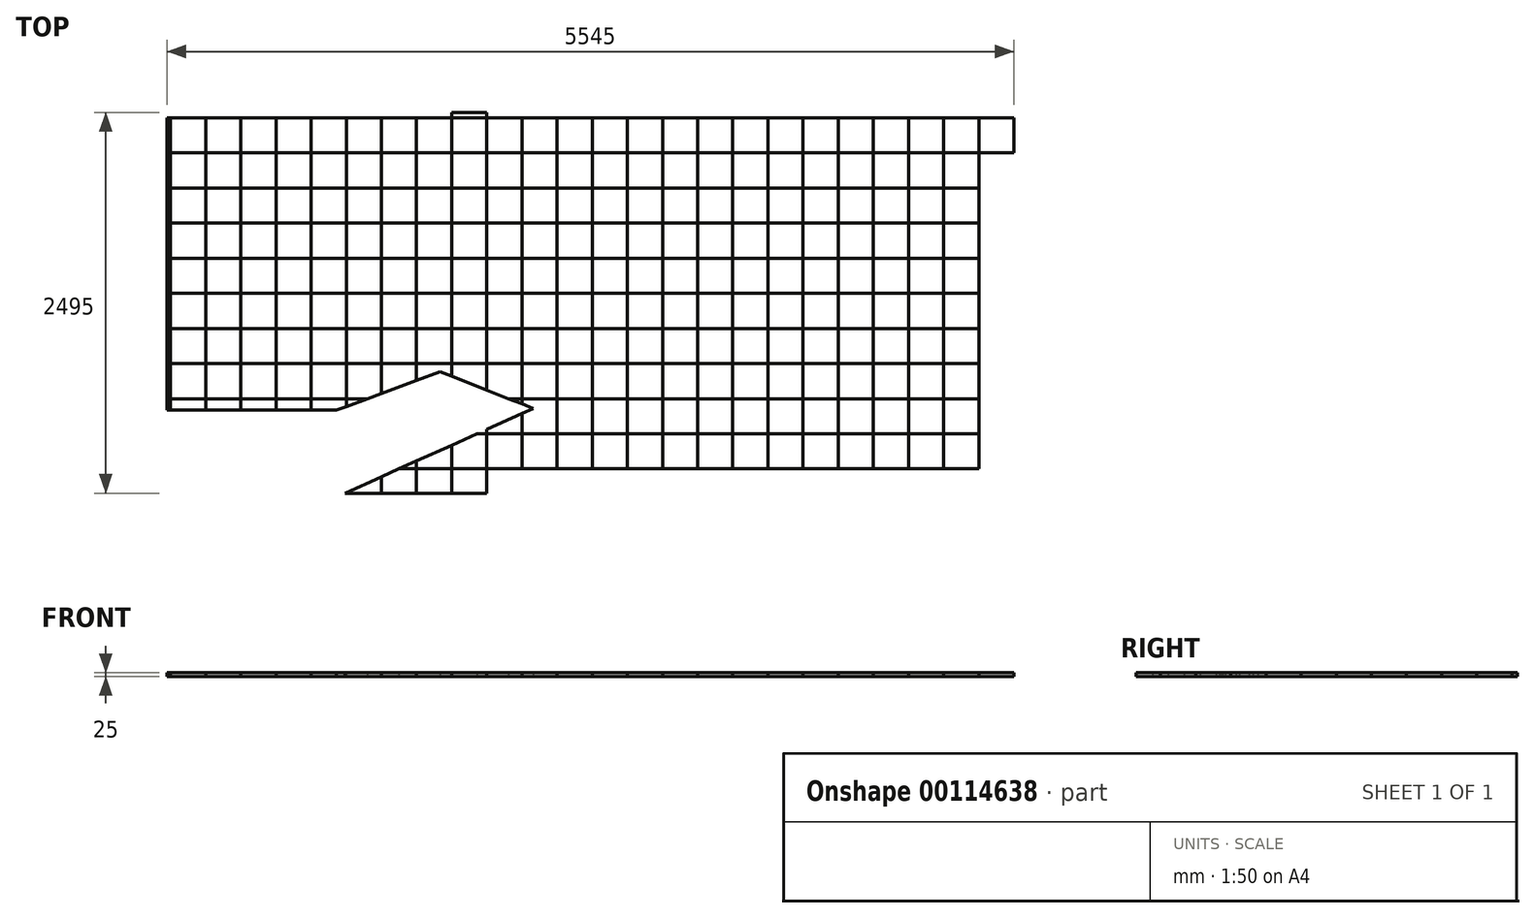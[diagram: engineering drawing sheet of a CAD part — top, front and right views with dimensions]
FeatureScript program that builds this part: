
annotation { "Feature Type Name" : "Feature", "Feature Type Description" : "" }
export const myFeature = defineFeature(function(context is Context, id is Id, definition is map)
    precondition{}
    {
        {
            var Q0;
            Q0=qCreatedBy(makeId("Top.planeOp"),FACE);
            var sketch = newSketch(context, id + "F0", { "sketchPlane" : qUnion([Q0])});
            skLineSegment(sketch, "E0.bottom", {"start": v(2772.5, -1247.5) * mm, "end": v(-1606.57, -1247.5) * mm});
            skLineSegment(sketch, "E0.top", {"start": v(2772.5, 1247.5) * mm, "end": v(-2772.5, 1247.5) * mm});
            skLineSegment(sketch, "E0.left", {"start": v(2772.5, -1247.5) * mm, "end": v(2772.5, 1247.5) * mm});
            skLineSegment(sketch, "E0.right", {"start": v(-2772.5, -702.5) * mm, "end": v(-2772.5, 1247.5) * mm});
            skPoint(sketch, "E0.middle", {"position": v(0, 0) * mm});
            skLineSegment(sketch, "E1", {"start": v(-2772.5, -702.5) * mm, "end": v(-1662.5, -702.5) * mm});
            skLineSegment(sketch, "E2", {"start": v(-1662.5, -702.5) * mm, "end": v(-982.3, -451.6) * mm});
            skLineSegment(sketch, "E3", {"start": v(-982.3, -451.6) * mm, "end": v(-372.7, -691.22) * mm});
            skLineSegment(sketch, "E4", {"start": v(-372.7, -691.22) * mm, "end": v(-1606.57, -1247.5) * mm});
            skPoint(sketch, "E5.orphan", {"position": v(-2772.5, -1247.5) * mm});
            skLineSegment(sketch, "E6.right", {"start": v(-2772.5, 1247.5) * mm, "end": v(-2772.5, 1217.5) * mm});
            skPoint(sketch, "E7.endSnap0", {"position": v(582.97, -1247.5) * mm});
            skLineSegment(sketch, "E8.bottom", {"start": v(-2772.5, 1247.5) * mm, "end": v(2772.5, 1247.5) * mm});
            skLineSegment(sketch, "E8.top", {"start": v(-2772.5, 1212.5) * mm, "end": v(2772.5, 1212.5) * mm});
            skLineSegment(sketch, "E8.left", {"start": v(-2772.5, 1247.5) * mm, "end": v(-2772.5, 1212.5) * mm});
            skLineSegment(sketch, "E8.right", {"start": v(2772.5, 1247.5) * mm, "end": v(2772.5, 1212.5) * mm});
            skLineSegment(sketch, "E9.bottom", {"start": v(2772.5, 1247.5) * mm, "end": v(2542.5, 1247.5) * mm});
            skLineSegment(sketch, "E9.top", {"start": v(2772.5, -1247.5) * mm, "end": v(2542.5, -1247.5) * mm});
            skLineSegment(sketch, "E9.left", {"start": v(2772.5, 1247.5) * mm, "end": v(2772.5, -1247.5) * mm});
            skLineSegment(sketch, "E9.right", {"start": v(2542.5, 1247.5) * mm, "end": v(2542.5, -1247.5) * mm});
            skLineSegment(sketch, "E10.bottom", {"start": v(2542.5, 1247.5) * mm, "end": v(2312.5, 1247.5) * mm});
            skLineSegment(sketch, "E10.top", {"start": v(2542.5, -1247.5) * mm, "end": v(2312.5, -1247.5) * mm});
            skLineSegment(sketch, "E10.right", {"start": v(2312.5, 1247.5) * mm, "end": v(2312.5, -1247.5) * mm});
            skLineSegment(sketch, "E11.bottom", {"start": v(2312.5, 1247.5) * mm, "end": v(2082.5, 1247.5) * mm});
            skLineSegment(sketch, "E11.top", {"start": v(2312.5, -1247.5) * mm, "end": v(2082.5, -1247.5) * mm});
            skLineSegment(sketch, "E11.right", {"start": v(2082.5, 1247.5) * mm, "end": v(2082.5, -1247.5) * mm});
            skLineSegment(sketch, "E12.bottom", {"start": v(2082.5, 1247.5) * mm, "end": v(1852.5, 1247.5) * mm});
            skLineSegment(sketch, "E12.top", {"start": v(2082.5, -1247.5) * mm, "end": v(1852.5, -1247.5) * mm});
            skLineSegment(sketch, "E12.right", {"start": v(1852.5, 1247.5) * mm, "end": v(1852.5, -1247.5) * mm});
            skLineSegment(sketch, "E13.bottom", {"start": v(1852.5, 1247.5) * mm, "end": v(1622.5, 1247.5) * mm});
            skLineSegment(sketch, "E13.top", {"start": v(1852.5, -1247.5) * mm, "end": v(1622.5, -1247.5) * mm});
            skLineSegment(sketch, "E13.right", {"start": v(1622.5, 1247.5) * mm, "end": v(1622.5, -1247.5) * mm});
            skLineSegment(sketch, "E14.bottom", {"start": v(1622.5, 1247.5) * mm, "end": v(1392.5, 1247.5) * mm});
            skLineSegment(sketch, "E14.top", {"start": v(1622.5, -1247.5) * mm, "end": v(1392.5, -1247.5) * mm});
            skLineSegment(sketch, "E14.right", {"start": v(1392.5, 1247.5) * mm, "end": v(1392.5, -1247.5) * mm});
            skLineSegment(sketch, "E15.bottom", {"start": v(1392.5, 1247.5) * mm, "end": v(1162.5, 1247.5) * mm});
            skLineSegment(sketch, "E15.top", {"start": v(1392.5, -1247.5) * mm, "end": v(1162.5, -1247.5) * mm});
            skLineSegment(sketch, "E15.right", {"start": v(1162.5, 1247.5) * mm, "end": v(1162.5, -1247.5) * mm});
            skLineSegment(sketch, "E16.bottom", {"start": v(1162.5, 1247.5) * mm, "end": v(932.5, 1247.5) * mm});
            skLineSegment(sketch, "E16.top", {"start": v(1162.5, -1247.5) * mm, "end": v(932.5, -1247.5) * mm});
            skLineSegment(sketch, "E16.right", {"start": v(932.5, 1247.5) * mm, "end": v(932.5, -1247.5) * mm});
            skLineSegment(sketch, "E17.bottom", {"start": v(932.5, 1247.5) * mm, "end": v(702.5, 1247.5) * mm});
            skLineSegment(sketch, "E17.top", {"start": v(932.5, -1247.5) * mm, "end": v(702.5, -1247.5) * mm});
            skLineSegment(sketch, "E17.right", {"start": v(702.5, 1247.5) * mm, "end": v(702.5, -1247.5) * mm});
            skLineSegment(sketch, "E18.bottom", {"start": v(702.5, 1247.5) * mm, "end": v(472.5, 1247.5) * mm});
            skLineSegment(sketch, "E18.top", {"start": v(702.5, -1247.5) * mm, "end": v(472.5, -1247.5) * mm});
            skLineSegment(sketch, "E18.right", {"start": v(472.5, 1247.5) * mm, "end": v(472.5, -1247.5) * mm});
            skLineSegment(sketch, "E19.bottom", {"start": v(472.5, 1247.5) * mm, "end": v(242.5, 1247.5) * mm});
            skLineSegment(sketch, "E19.top", {"start": v(472.5, -1247.5) * mm, "end": v(242.5, -1247.5) * mm});
            skLineSegment(sketch, "E19.right", {"start": v(242.5, 1247.5) * mm, "end": v(242.5, -1247.5) * mm});
            skLineSegment(sketch, "E20.bottom", {"start": v(242.5, 1247.5) * mm, "end": v(12.5, 1247.5) * mm});
            skLineSegment(sketch, "E20.top", {"start": v(242.5, -1247.5) * mm, "end": v(12.5, -1247.5) * mm});
            skLineSegment(sketch, "E20.right", {"start": v(12.5, 1247.5) * mm, "end": v(12.5, -1247.5) * mm});
            skLineSegment(sketch, "E21.bottom", {"start": v(12.5, 1247.5) * mm, "end": v(-217.5, 1247.5) * mm});
            skLineSegment(sketch, "E21.top", {"start": v(12.5, -1247.5) * mm, "end": v(-217.5, -1247.5) * mm});
            skLineSegment(sketch, "E21.right", {"start": v(-217.5, 1247.5) * mm, "end": v(-217.5, -1247.5) * mm});
            skLineSegment(sketch, "E22.bottom", {"start": v(-217.5, 1247.5) * mm, "end": v(-447.5, 1247.5) * mm});
            skLineSegment(sketch, "E22.top", {"start": v(-217.5, -1247.5) * mm, "end": v(-447.5, -1247.5) * mm});
            skLineSegment(sketch, "E22.right", {"start": v(-447.5, 1247.5) * mm, "end": v(-447.5, -661.81) * mm});
            skPoint(sketch, "E23.oppositeSnap0", {"position": v(-677.5, -571.4) * mm});
            skLineSegment(sketch, "E23.bottom", {"start": v(-447.5, 1247.5) * mm, "end": v(-677.5, 1247.5) * mm});
            skLineSegment(sketch, "E23.top", {"start": v(-447.5, -1247.5) * mm, "end": v(-677.5, -1247.5) * mm});
            skLineSegment(sketch, "E23.right", {"start": v(-677.5, 1247.5) * mm, "end": v(-677.5, -397.5) * mm});
            skLineSegment(sketch, "E24", {"start": v(-2772.5, 982.5) * mm, "end": v(2772.5, 982.5) * mm});
            skLineSegment(sketch, "E25", {"start": v(-2772.5, 752.5) * mm, "end": v(2772.5, 752.5) * mm});
            skLineSegment(sketch, "E26", {"start": v(-2772.5, 522.5) * mm, "end": v(2772.5, 522.5) * mm});
            skLineSegment(sketch, "E27", {"start": v(-2772.5, 292.5) * mm, "end": v(2772.5, 292.5) * mm});
            skLineSegment(sketch, "E28", {"start": v(-2772.5, 62.5) * mm, "end": v(2772.5, 62.5) * mm});
            skLineSegment(sketch, "E29", {"start": v(2772.5, -167.5) * mm, "end": v(-2772.5, -167.5) * mm});
            skLineSegment(sketch, "E30", {"start": v(-1251.68, -1087.5) * mm, "end": v(2772.5, -1087.5) * mm});
            skLineSegment(sketch, "E31", {"start": v(-741.53, -857.5) * mm, "end": v(2772.5, -857.5) * mm});
            skLineSegment(sketch, "E32", {"start": v(-534.8, -627.5) * mm, "end": v(2772.5, -627.5) * mm});
            skLineSegment(sketch, "E33", {"start": v(-2772.5, -397.5) * mm, "end": v(2772.5, -397.5) * mm});
            skLineSegment(sketch, "E34", {"start": v(-2057.5, 1247.5) * mm, "end": v(-2057.5, -702.5) * mm});
            skLineSegment(sketch, "E35", {"start": v(-1827.5, 1247.5) * mm, "end": v(-1827.5, -702.5) * mm});
            skLineSegment(sketch, "E36", {"start": v(-1597.5, 1247.5) * mm, "end": v(-1597.5, -702.5) * mm});
            skLineSegment(sketch, "E37", {"start": v(-1367.5, 1247.5) * mm, "end": v(-1367.5, -593.69) * mm});
            skLineSegment(sketch, "E38", {"start": v(-1137.5, 1247.5) * mm, "end": v(-1137.5, -508.85) * mm});
            skLineSegment(sketch, "E39", {"start": v(-2517.5, -702.5) * mm, "end": v(-2517.5, 1247.5) * mm});
            skLineSegment(sketch, "E40", {"start": v(-2287.5, 1247.5) * mm, "end": v(-2287.5, -702.5) * mm});
            skLineSegment(sketch, "E41", {"start": v(-2747.5, 1247.5) * mm, "end": v(-2747.5, -702.5) * mm});
            skLineSegment(sketch, "E42.trimOffspring", {"start": v(-677.5, -828.63) * mm, "end": v(-677.5, -1247.5) * mm});
            skLineSegment(sketch, "E43.trimOffspring", {"start": v(-447.5, -724.94) * mm, "end": v(-447.5, -1247.5) * mm});
            skLineSegment(sketch, "E44", {"start": v(-677.5, -571.4) * mm, "end": v(-677.5, -397.5) * mm});
            skLineSegment(sketch, "E45", {"start": v(-907.5, -481) * mm, "end": v(-907.5, 1247.5) * mm});
            skLineSegment(sketch, "E46", {"start": v(-2772.5, -627.5) * mm, "end": v(-1459.17, -627.5) * mm});
            skLineSegment(sketch, "E47", {"start": v(-907.5, -932.33) * mm, "end": v(-907.5, -1247.5) * mm});
            skLineSegment(sketch, "E48", {"start": v(-1137.5, -1036.02) * mm, "end": v(-1137.5, -1247.5) * mm});
            skLineSegment(sketch, "E49", {"start": v(-1367.5, -1139.72) * mm, "end": v(-1367.5, -1247.5) * mm});
            skSolve(sketch);
        }
        {
            var Q0;
            {var subQ5=sQuery(id+"F0.wireOp",EDGE,"E9.bottom");Q0=makeQuery(id+"F0.imprint","IMPRINT",FACE,{"disambiguationData":[TD([[makeQuery(id+"F0.imprint","IMPRINT",EDGE,{"derivedFrom":subQ5}),1.0]])]});}
            var Q1;
            {var subQ0=sQuery(id+"F0.wireOp",EDGE,"E10.right");var subQ1=sQuery(id+"F0.wireOp",EDGE,"E8.top");var subQ2=makeQuery(id+"F0.imprint","INTERSECT",VERTEX,{"derivedFrom":[subQ1,subQ0]});Q1=makeQuery(id+"F0.imprint","IMPRINT",FACE,{"disambiguationData":[TD([[makeQuery(id+"F0.imprint","IMPRINT",EDGE,{"disambiguationData":[TD([[subQ2,-1.0]])],"derivedFrom":subQ1}),-1.0]])]});}
            var Q2;
            {var subQ0=sQuery(id+"F0.wireOp",EDGE,"E24");var subQ1=sQuery(id+"F0.wireOp",EDGE,"E10.right");var subQ2=makeQuery(id+"F0.imprint","INTERSECT",VERTEX,{"derivedFrom":[subQ1,subQ0]});Q2=makeQuery(id+"F0.imprint","IMPRINT",FACE,{"disambiguationData":[TD([[makeQuery(id+"F0.imprint","IMPRINT",EDGE,{"disambiguationData":[TD([[subQ2,-1.0]])],"derivedFrom":subQ1}),-1.0]])]});}
            var Q3;
            {var subQ0=sQuery(id+"F0.wireOp",EDGE,"E25");var subQ1=sQuery(id+"F0.wireOp",EDGE,"E11.right");var subQ2=makeQuery(id+"F0.imprint","INTERSECT",VERTEX,{"derivedFrom":[subQ1,subQ0]});Q3=makeQuery(id+"F0.imprint","IMPRINT",FACE,{"disambiguationData":[TD([[makeQuery(id+"F0.imprint","IMPRINT",EDGE,{"disambiguationData":[TD([[subQ2,-1.0]])],"derivedFrom":subQ1}),-1.0]])]});}
            var Q4;
            {var subQ0=sQuery(id+"F0.wireOp",EDGE,"E26");var subQ1=sQuery(id+"F0.wireOp",EDGE,"E12.right");var subQ2=makeQuery(id+"F0.imprint","INTERSECT",VERTEX,{"derivedFrom":[subQ1,subQ0]});Q4=makeQuery(id+"F0.imprint","IMPRINT",FACE,{"disambiguationData":[TD([[makeQuery(id+"F0.imprint","IMPRINT",EDGE,{"disambiguationData":[TD([[subQ2,-1.0]])],"derivedFrom":subQ1}),-1.0]])]});}
            var Q5;
            {var subQ0=sQuery(id+"F0.wireOp",EDGE,"E29");var subQ1=sQuery(id+"F0.wireOp",EDGE,"E15.right");var subQ2=makeQuery(id+"F0.imprint","INTERSECT",VERTEX,{"derivedFrom":[subQ1,subQ0]});Q5=makeQuery(id+"F0.imprint","IMPRINT",FACE,{"disambiguationData":[TD([[makeQuery(id+"F0.imprint","IMPRINT",EDGE,{"disambiguationData":[TD([[subQ2,-1.0]])],"derivedFrom":subQ1}),-1.0]])]});}
            var Q6;
            {var subQ0=sQuery(id+"F0.wireOp",EDGE,"E33");var subQ1=sQuery(id+"F0.wireOp",EDGE,"E16.right");var subQ2=makeQuery(id+"F0.imprint","INTERSECT",VERTEX,{"derivedFrom":[subQ1,subQ0]});Q6=makeQuery(id+"F0.imprint","IMPRINT",FACE,{"disambiguationData":[TD([[makeQuery(id+"F0.imprint","IMPRINT",EDGE,{"disambiguationData":[TD([[subQ2,-1.0]])],"derivedFrom":subQ1}),-1.0]])]});}
            var Q7;
            {var subQ0=sQuery(id+"F0.wireOp",EDGE,"E27");var subQ1=sQuery(id+"F0.wireOp",EDGE,"E13.right");var subQ2=makeQuery(id+"F0.imprint","INTERSECT",VERTEX,{"derivedFrom":[subQ1,subQ0]});Q7=makeQuery(id+"F0.imprint","IMPRINT",FACE,{"disambiguationData":[TD([[makeQuery(id+"F0.imprint","IMPRINT",EDGE,{"disambiguationData":[TD([[subQ2,-1.0]])],"derivedFrom":subQ1}),-1.0]])]});}
            var Q8;
            {var subQ0=sQuery(id+"F0.wireOp",EDGE,"E24");var subQ1=sQuery(id+"F0.wireOp",EDGE,"E9.left");var subQ2=makeQuery(id+"F0.imprint","INTERSECT",VERTEX,{"derivedFrom":[subQ1,subQ0]});Q8=makeQuery(id+"F0.imprint","IMPRINT",FACE,{"disambiguationData":[TD([[makeQuery(id+"F0.imprint","IMPRINT",EDGE,{"disambiguationData":[TD([[subQ2,-1.0]])],"derivedFrom":subQ1}),-1.0]])]});}
            var Q9;
            {var subQ0=sQuery(id+"F0.wireOp",EDGE,"E25");var subQ1=sQuery(id+"F0.wireOp",EDGE,"E9.right");var subQ2=makeQuery(id+"F0.imprint","INTERSECT",VERTEX,{"derivedFrom":[subQ1,subQ0]});Q9=makeQuery(id+"F0.imprint","IMPRINT",FACE,{"disambiguationData":[TD([[makeQuery(id+"F0.imprint","IMPRINT",EDGE,{"disambiguationData":[TD([[subQ2,-1.0]])],"derivedFrom":subQ1}),-1.0]])]});}
            var Q10;
            {var subQ0=sQuery(id+"F0.wireOp",EDGE,"E26");var subQ1=sQuery(id+"F0.wireOp",EDGE,"E10.right");var subQ2=makeQuery(id+"F0.imprint","INTERSECT",VERTEX,{"derivedFrom":[subQ1,subQ0]});Q10=makeQuery(id+"F0.imprint","IMPRINT",FACE,{"disambiguationData":[TD([[makeQuery(id+"F0.imprint","IMPRINT",EDGE,{"disambiguationData":[TD([[subQ2,-1.0]])],"derivedFrom":subQ1}),-1.0]])]});}
            var Q11;
            {var subQ0=sQuery(id+"F0.wireOp",EDGE,"E27");var subQ1=sQuery(id+"F0.wireOp",EDGE,"E11.right");var subQ2=makeQuery(id+"F0.imprint","INTERSECT",VERTEX,{"derivedFrom":[subQ1,subQ0]});Q11=makeQuery(id+"F0.imprint","IMPRINT",FACE,{"disambiguationData":[TD([[makeQuery(id+"F0.imprint","IMPRINT",EDGE,{"disambiguationData":[TD([[subQ2,-1.0]])],"derivedFrom":subQ1}),-1.0]])]});}
            var Q12;
            {var subQ0=sQuery(id+"F0.wireOp",EDGE,"E28");var subQ1=sQuery(id+"F0.wireOp",EDGE,"E12.right");var subQ2=makeQuery(id+"F0.imprint","INTERSECT",VERTEX,{"derivedFrom":[subQ1,subQ0]});Q12=makeQuery(id+"F0.imprint","IMPRINT",FACE,{"disambiguationData":[TD([[makeQuery(id+"F0.imprint","IMPRINT",EDGE,{"disambiguationData":[TD([[subQ2,-1.0]])],"derivedFrom":subQ1}),-1.0]])]});}
            var Q13;
            {var subQ0=sQuery(id+"F0.wireOp",EDGE,"E29");var subQ1=sQuery(id+"F0.wireOp",EDGE,"E13.right");var subQ2=makeQuery(id+"F0.imprint","INTERSECT",VERTEX,{"derivedFrom":[subQ1,subQ0]});Q13=makeQuery(id+"F0.imprint","IMPRINT",FACE,{"disambiguationData":[TD([[makeQuery(id+"F0.imprint","IMPRINT",EDGE,{"disambiguationData":[TD([[subQ2,-1.0]])],"derivedFrom":subQ1}),-1.0]])]});}
            var Q14;
            {var subQ0=sQuery(id+"F0.wireOp",EDGE,"E28");var subQ1=sQuery(id+"F0.wireOp",EDGE,"E14.right");var subQ2=makeQuery(id+"F0.imprint","INTERSECT",VERTEX,{"derivedFrom":[subQ1,subQ0]});Q14=makeQuery(id+"F0.imprint","IMPRINT",FACE,{"disambiguationData":[TD([[makeQuery(id+"F0.imprint","IMPRINT",EDGE,{"disambiguationData":[TD([[subQ2,-1.0]])],"derivedFrom":subQ1}),-1.0]])]});}
            var Q15;
            {var subQ0=sQuery(id+"F0.wireOp",EDGE,"E33");var subQ1=sQuery(id+"F0.wireOp",EDGE,"E14.right");var subQ2=makeQuery(id+"F0.imprint","INTERSECT",VERTEX,{"derivedFrom":[subQ1,subQ0]});Q15=makeQuery(id+"F0.imprint","IMPRINT",FACE,{"disambiguationData":[TD([[makeQuery(id+"F0.imprint","IMPRINT",EDGE,{"disambiguationData":[TD([[subQ2,-1.0]])],"derivedFrom":subQ1}),-1.0]])]});}
            var Q16;
            {var subQ0=sQuery(id+"F0.wireOp",EDGE,"E33");var subQ1=sQuery(id+"F0.wireOp",EDGE,"E12.right");var subQ2=makeQuery(id+"F0.imprint","INTERSECT",VERTEX,{"derivedFrom":[subQ1,subQ0]});Q16=makeQuery(id+"F0.imprint","IMPRINT",FACE,{"disambiguationData":[TD([[makeQuery(id+"F0.imprint","IMPRINT",EDGE,{"disambiguationData":[TD([[subQ2,-1.0]])],"derivedFrom":subQ1}),-1.0]])]});}
            var Q17;
            {var subQ0=sQuery(id+"F0.wireOp",EDGE,"E33");var subQ1=sQuery(id+"F0.wireOp",EDGE,"E10.right");var subQ2=makeQuery(id+"F0.imprint","INTERSECT",VERTEX,{"derivedFrom":[subQ1,subQ0]});Q17=makeQuery(id+"F0.imprint","IMPRINT",FACE,{"disambiguationData":[TD([[makeQuery(id+"F0.imprint","IMPRINT",EDGE,{"disambiguationData":[TD([[subQ2,-1.0]])],"derivedFrom":subQ1}),-1.0]])]});}
            var Q18;
            {var subQ0=sQuery(id+"F0.wireOp",EDGE,"E32");var subQ1=sQuery(id+"F0.wireOp",EDGE,"E9.left");var subQ2=makeQuery(id+"F0.imprint","INTERSECT",VERTEX,{"derivedFrom":[subQ1,subQ0]});Q18=makeQuery(id+"F0.imprint","IMPRINT",FACE,{"disambiguationData":[TD([[makeQuery(id+"F0.imprint","IMPRINT",EDGE,{"disambiguationData":[TD([[subQ2,1.0]])],"derivedFrom":subQ1}),-1.0]])]});}
            var Q19;
            {var subQ0=sQuery(id+"F0.wireOp",EDGE,"E29");var subQ1=sQuery(id+"F0.wireOp",EDGE,"E9.right");var subQ2=makeQuery(id+"F0.imprint","INTERSECT",VERTEX,{"derivedFrom":[subQ1,subQ0]});Q19=makeQuery(id+"F0.imprint","IMPRINT",FACE,{"disambiguationData":[TD([[makeQuery(id+"F0.imprint","IMPRINT",EDGE,{"disambiguationData":[TD([[subQ2,-1.0]])],"derivedFrom":subQ1}),-1.0]])]});}
            var Q20;
            {var subQ0=sQuery(id+"F0.wireOp",EDGE,"E28");var subQ1=sQuery(id+"F0.wireOp",EDGE,"E10.right");var subQ2=makeQuery(id+"F0.imprint","INTERSECT",VERTEX,{"derivedFrom":[subQ1,subQ0]});Q20=makeQuery(id+"F0.imprint","IMPRINT",FACE,{"disambiguationData":[TD([[makeQuery(id+"F0.imprint","IMPRINT",EDGE,{"disambiguationData":[TD([[subQ2,-1.0]])],"derivedFrom":subQ1}),-1.0]])]});}
            var Q21;
            {var subQ0=sQuery(id+"F0.wireOp",EDGE,"E29");var subQ1=sQuery(id+"F0.wireOp",EDGE,"E11.right");var subQ2=makeQuery(id+"F0.imprint","INTERSECT",VERTEX,{"derivedFrom":[subQ1,subQ0]});Q21=makeQuery(id+"F0.imprint","IMPRINT",FACE,{"disambiguationData":[TD([[makeQuery(id+"F0.imprint","IMPRINT",EDGE,{"disambiguationData":[TD([[subQ2,-1.0]])],"derivedFrom":subQ1}),-1.0]])]});}
            var Q22;
            {var subQ0=sQuery(id+"F0.wireOp",EDGE,"E27");var subQ1=sQuery(id+"F0.wireOp",EDGE,"E9.right");var subQ2=makeQuery(id+"F0.imprint","INTERSECT",VERTEX,{"derivedFrom":[subQ1,subQ0]});Q22=makeQuery(id+"F0.imprint","IMPRINT",FACE,{"disambiguationData":[TD([[makeQuery(id+"F0.imprint","IMPRINT",EDGE,{"disambiguationData":[TD([[subQ2,-1.0]])],"derivedFrom":subQ1}),-1.0]])]});}
            var Q23;
            {var subQ0=sQuery(id+"F0.wireOp",EDGE,"E26");var subQ1=sQuery(id+"F0.wireOp",EDGE,"E9.left");var subQ2=makeQuery(id+"F0.imprint","INTERSECT",VERTEX,{"derivedFrom":[subQ1,subQ0]});Q23=makeQuery(id+"F0.imprint","IMPRINT",FACE,{"disambiguationData":[TD([[makeQuery(id+"F0.imprint","IMPRINT",EDGE,{"disambiguationData":[TD([[subQ2,-1.0]])],"derivedFrom":subQ1}),-1.0]])]});}
            var Q24;
            {var subQ0=sQuery(id+"F0.wireOp",EDGE,"E28");var subQ1=sQuery(id+"F0.wireOp",EDGE,"E9.left");var subQ2=makeQuery(id+"F0.imprint","INTERSECT",VERTEX,{"derivedFrom":[subQ1,subQ0]});Q24=makeQuery(id+"F0.imprint","IMPRINT",FACE,{"disambiguationData":[TD([[makeQuery(id+"F0.imprint","IMPRINT",EDGE,{"disambiguationData":[TD([[subQ2,-1.0]])],"derivedFrom":subQ1}),-1.0]])]});}
            var Q25;
            {var subQ0=sQuery(id+"F0.wireOp",EDGE,"E32");var subQ1=sQuery(id+"F0.wireOp",EDGE,"E9.right");var subQ2=makeQuery(id+"F0.imprint","INTERSECT",VERTEX,{"derivedFrom":[subQ1,subQ0]});Q25=makeQuery(id+"F0.imprint","IMPRINT",FACE,{"disambiguationData":[TD([[makeQuery(id+"F0.imprint","IMPRINT",EDGE,{"disambiguationData":[TD([[subQ2,-1.0]])],"derivedFrom":subQ1}),-1.0]])]});}
            var Q26;
            {var subQ0=sQuery(id+"F0.wireOp",EDGE,"E31");var subQ1=sQuery(id+"F0.wireOp",EDGE,"E10.right");var subQ2=makeQuery(id+"F0.imprint","INTERSECT",VERTEX,{"derivedFrom":[subQ1,subQ0]});Q26=makeQuery(id+"F0.imprint","IMPRINT",FACE,{"disambiguationData":[TD([[makeQuery(id+"F0.imprint","IMPRINT",EDGE,{"disambiguationData":[TD([[subQ2,-1.0]])],"derivedFrom":subQ1}),-1.0]])]});}
            var Q27;
            {var subQ0=sQuery(id+"F0.wireOp",EDGE,"E12.top");Q27=makeQuery(id+"F0.imprint","IMPRINT",FACE,{"disambiguationData":[TD([[makeQuery(id+"F0.imprint","IMPRINT",EDGE,{"derivedFrom":subQ0}),-1.0]])]});}
            var Q28;
            {var subQ0=sQuery(id+"F0.wireOp",EDGE,"E30");var subQ1=sQuery(id+"F0.wireOp",EDGE,"E9.left");var subQ2=makeQuery(id+"F0.imprint","INTERSECT",VERTEX,{"derivedFrom":[subQ1,subQ0]});Q28=makeQuery(id+"F0.imprint","IMPRINT",FACE,{"disambiguationData":[TD([[makeQuery(id+"F0.imprint","IMPRINT",EDGE,{"disambiguationData":[TD([[subQ2,1.0]])],"derivedFrom":subQ1}),-1.0]])]});}
            var Q29;
            {var subQ0=sQuery(id+"F0.wireOp",EDGE,"E10.top");Q29=makeQuery(id+"F0.imprint","IMPRINT",FACE,{"disambiguationData":[TD([[makeQuery(id+"F0.imprint","IMPRINT",EDGE,{"derivedFrom":subQ0}),-1.0]])]});}
            var Q30;
            {var subQ0=sQuery(id+"F0.wireOp",EDGE,"E32");var subQ1=sQuery(id+"F0.wireOp",EDGE,"E11.right");var subQ2=makeQuery(id+"F0.imprint","INTERSECT",VERTEX,{"derivedFrom":[subQ1,subQ0]});Q30=makeQuery(id+"F0.imprint","IMPRINT",FACE,{"disambiguationData":[TD([[makeQuery(id+"F0.imprint","IMPRINT",EDGE,{"disambiguationData":[TD([[subQ2,-1.0]])],"derivedFrom":subQ1}),-1.0]])]});}
            var Q31;
            {var subQ0=sQuery(id+"F0.wireOp",EDGE,"E31");var subQ1=sQuery(id+"F0.wireOp",EDGE,"E12.right");var subQ2=makeQuery(id+"F0.imprint","INTERSECT",VERTEX,{"derivedFrom":[subQ1,subQ0]});Q31=makeQuery(id+"F0.imprint","IMPRINT",FACE,{"disambiguationData":[TD([[makeQuery(id+"F0.imprint","IMPRINT",EDGE,{"disambiguationData":[TD([[subQ2,-1.0]])],"derivedFrom":subQ1}),-1.0]])]});}
            var Q32;
            {var subQ0=sQuery(id+"F0.wireOp",EDGE,"E32");var subQ1=sQuery(id+"F0.wireOp",EDGE,"E13.right");var subQ2=makeQuery(id+"F0.imprint","INTERSECT",VERTEX,{"derivedFrom":[subQ1,subQ0]});Q32=makeQuery(id+"F0.imprint","IMPRINT",FACE,{"disambiguationData":[TD([[makeQuery(id+"F0.imprint","IMPRINT",EDGE,{"disambiguationData":[TD([[subQ2,-1.0]])],"derivedFrom":subQ1}),-1.0]])]});}
            var Q33;
            {var subQ0=sQuery(id+"F0.wireOp",EDGE,"E31");var subQ1=sQuery(id+"F0.wireOp",EDGE,"E14.right");var subQ2=makeQuery(id+"F0.imprint","INTERSECT",VERTEX,{"derivedFrom":[subQ1,subQ0]});Q33=makeQuery(id+"F0.imprint","IMPRINT",FACE,{"disambiguationData":[TD([[makeQuery(id+"F0.imprint","IMPRINT",EDGE,{"disambiguationData":[TD([[subQ2,-1.0]])],"derivedFrom":subQ1}),-1.0]])]});}
            var Q34;
            {var subQ0=sQuery(id+"F0.wireOp",EDGE,"E16.top");Q34=makeQuery(id+"F0.imprint","IMPRINT",FACE,{"disambiguationData":[TD([[makeQuery(id+"F0.imprint","IMPRINT",EDGE,{"derivedFrom":subQ0}),-1.0]])]});}
            var Q35;
            {var subQ0=sQuery(id+"F0.wireOp",EDGE,"E32");var subQ1=sQuery(id+"F0.wireOp",EDGE,"E15.right");var subQ2=makeQuery(id+"F0.imprint","INTERSECT",VERTEX,{"derivedFrom":[subQ1,subQ0]});Q35=makeQuery(id+"F0.imprint","IMPRINT",FACE,{"disambiguationData":[TD([[makeQuery(id+"F0.imprint","IMPRINT",EDGE,{"disambiguationData":[TD([[subQ2,-1.0]])],"derivedFrom":subQ1}),-1.0]])]});}
            var Q36;
            {var subQ0=sQuery(id+"F0.wireOp",EDGE,"E31");var subQ1=sQuery(id+"F0.wireOp",EDGE,"E16.right");var subQ2=makeQuery(id+"F0.imprint","INTERSECT",VERTEX,{"derivedFrom":[subQ1,subQ0]});Q36=makeQuery(id+"F0.imprint","IMPRINT",FACE,{"disambiguationData":[TD([[makeQuery(id+"F0.imprint","IMPRINT",EDGE,{"disambiguationData":[TD([[subQ2,-1.0]])],"derivedFrom":subQ1}),-1.0]])]});}
            var Q37;
            {var subQ0=sQuery(id+"F0.wireOp",EDGE,"E18.top");Q37=makeQuery(id+"F0.imprint","IMPRINT",FACE,{"disambiguationData":[TD([[makeQuery(id+"F0.imprint","IMPRINT",EDGE,{"derivedFrom":subQ0}),-1.0]])]});}
            var Q38;
            {var subQ0=sQuery(id+"F0.wireOp",EDGE,"E20.top");Q38=makeQuery(id+"F0.imprint","IMPRINT",FACE,{"disambiguationData":[TD([[makeQuery(id+"F0.imprint","IMPRINT",EDGE,{"derivedFrom":subQ0}),-1.0]])]});}
            var Q39;
            {var subQ0=sQuery(id+"F0.wireOp",EDGE,"E22.top");Q39=makeQuery(id+"F0.imprint","IMPRINT",FACE,{"disambiguationData":[TD([[makeQuery(id+"F0.imprint","IMPRINT",EDGE,{"derivedFrom":subQ0}),-1.0]])]});}
            var Q40;
            {var subQ3=sQuery(id+"F0.wireOp",EDGE,"E47");var subQ5=sQuery(id+"F0.wireOp",EDGE,"E30");var subQ6=makeQuery(id+"F0.imprint","INTERSECT",VERTEX,{"derivedFrom":[subQ5,subQ3]});Q40=makeQuery(id+"F0.imprint","IMPRINT",FACE,{"disambiguationData":[TD([[makeQuery(id+"F0.imprint","IMPRINT",EDGE,{"disambiguationData":[TD([[subQ6,-1.0]])],"derivedFrom":subQ5}),-1.0]])]});}
            var Q41;
            {var subQ0=sQuery(id+"F0.wireOp",EDGE,"E31");var subQ1=sQuery(id+"F0.wireOp",EDGE,"E18.right");var subQ2=makeQuery(id+"F0.imprint","INTERSECT",VERTEX,{"derivedFrom":[subQ1,subQ0]});Q41=makeQuery(id+"F0.imprint","IMPRINT",FACE,{"disambiguationData":[TD([[makeQuery(id+"F0.imprint","IMPRINT",EDGE,{"disambiguationData":[TD([[subQ2,-1.0]])],"derivedFrom":subQ1}),-1.0]])]});}
            var Q42;
            {var subQ0=sQuery(id+"F0.wireOp",EDGE,"E32");var subQ1=sQuery(id+"F0.wireOp",EDGE,"E17.right");var subQ2=makeQuery(id+"F0.imprint","INTERSECT",VERTEX,{"derivedFrom":[subQ1,subQ0]});Q42=makeQuery(id+"F0.imprint","IMPRINT",FACE,{"disambiguationData":[TD([[makeQuery(id+"F0.imprint","IMPRINT",EDGE,{"disambiguationData":[TD([[subQ2,-1.0]])],"derivedFrom":subQ1}),-1.0]])]});}
            var Q43;
            {var subQ0=sQuery(id+"F0.wireOp",EDGE,"E31");var subQ1=sQuery(id+"F0.wireOp",EDGE,"E20.right");var subQ2=makeQuery(id+"F0.imprint","INTERSECT",VERTEX,{"derivedFrom":[subQ1,subQ0]});Q43=makeQuery(id+"F0.imprint","IMPRINT",FACE,{"disambiguationData":[TD([[makeQuery(id+"F0.imprint","IMPRINT",EDGE,{"disambiguationData":[TD([[subQ2,-1.0]])],"derivedFrom":subQ1}),-1.0]])]});}
            var Q44;
            {var subQ0=sQuery(id+"F0.wireOp",EDGE,"E42.trimOffspring");var subQ1=sQuery(id+"F0.wireOp",EDGE,"E30");var subQ2=makeQuery(id+"F0.imprint","INTERSECT",VERTEX,{"derivedFrom":[subQ1,subQ0]});Q44=makeQuery(id+"F0.imprint","IMPRINT",FACE,{"disambiguationData":[TD([[makeQuery(id+"F0.imprint","IMPRINT",EDGE,{"disambiguationData":[TD([[subQ2,-1.0]])],"derivedFrom":subQ1}),1.0]])]});}
            var Q45;
            {var subQ0=sQuery(id+"F0.wireOp",EDGE,"E47");var subQ1=sQuery(id+"F0.wireOp",EDGE,"E4");var subQ2=makeQuery(id+"F0.imprint","INTERSECT",VERTEX,{"derivedFrom":[subQ1,subQ0]});Q45=makeQuery(id+"F0.imprint","IMPRINT",FACE,{"disambiguationData":[TD([[makeQuery(id+"F0.imprint","IMPRINT",EDGE,{"disambiguationData":[TD([[subQ2,-1.0]])],"derivedFrom":subQ1}),1.0]])]});}
            var Q46;
            {var subQ7=sQuery(id+"F0.wireOp",EDGE,"E49");Q46=makeQuery(id+"F0.imprint","IMPRINT",FACE,{"disambiguationData":[TD([[makeQuery(id+"F0.imprint","IMPRINT",EDGE,{"derivedFrom":subQ7}),1.0]])]});}
            var Q47;
            {var subQ1=sQuery(id+"F0.wireOp",EDGE,"E3");var subQ6=sQuery(id+"F0.wireOp",EDGE,"E4");var subQ13=makeQuery(id+"F0.imprint","INTERSECT",VERTEX,{"derivedFrom":[subQ1,subQ6]});Q47=makeQuery(id+"F0.imprint","IMPRINT",FACE,{"disambiguationData":[TD([[makeQuery(id+"F0.imprint","IMPRINT",EDGE,{"disambiguationData":[TD([[subQ13,1.0]])],"derivedFrom":subQ1}),1.0]])]});}
            var Q48;
            {var subQ0=sQuery(id+"F0.wireOp",EDGE,"E32");var subQ1=sQuery(id+"F0.wireOp",EDGE,"E19.right");var subQ2=makeQuery(id+"F0.imprint","INTERSECT",VERTEX,{"derivedFrom":[subQ1,subQ0]});Q48=makeQuery(id+"F0.imprint","IMPRINT",FACE,{"disambiguationData":[TD([[makeQuery(id+"F0.imprint","IMPRINT",EDGE,{"disambiguationData":[TD([[subQ2,-1.0]])],"derivedFrom":subQ1}),-1.0]])]});}
            var Q49;
            {var subQ0=sQuery(id+"F0.wireOp",EDGE,"E33");var subQ1=sQuery(id+"F0.wireOp",EDGE,"E18.right");var subQ2=makeQuery(id+"F0.imprint","INTERSECT",VERTEX,{"derivedFrom":[subQ1,subQ0]});Q49=makeQuery(id+"F0.imprint","IMPRINT",FACE,{"disambiguationData":[TD([[makeQuery(id+"F0.imprint","IMPRINT",EDGE,{"disambiguationData":[TD([[subQ2,-1.0]])],"derivedFrom":subQ1}),-1.0]])]});}
            var Q50;
            {var subQ0=sQuery(id+"F0.wireOp",EDGE,"E33");var subQ1=sQuery(id+"F0.wireOp",EDGE,"E20.right");var subQ2=makeQuery(id+"F0.imprint","INTERSECT",VERTEX,{"derivedFrom":[subQ1,subQ0]});Q50=makeQuery(id+"F0.imprint","IMPRINT",FACE,{"disambiguationData":[TD([[makeQuery(id+"F0.imprint","IMPRINT",EDGE,{"disambiguationData":[TD([[subQ2,-1.0]])],"derivedFrom":subQ1}),-1.0]])]});}
            var Q51;
            {var subQ5=sQuery(id+"F0.wireOp",EDGE,"E44");Q51=makeQuery(id+"F0.imprint","IMPRINT",FACE,{"disambiguationData":[TD([[makeQuery(id+"F0.imprint","IMPRINT",EDGE,{"derivedFrom":subQ5}),-1.0]])]});}
            var Q52;
            {var subQ0=sQuery(id+"F0.wireOp",EDGE,"E29");var subQ1=sQuery(id+"F0.wireOp",EDGE,"E19.right");var subQ2=makeQuery(id+"F0.imprint","INTERSECT",VERTEX,{"derivedFrom":[subQ1,subQ0]});Q52=makeQuery(id+"F0.imprint","IMPRINT",FACE,{"disambiguationData":[TD([[makeQuery(id+"F0.imprint","IMPRINT",EDGE,{"disambiguationData":[TD([[subQ2,-1.0]])],"derivedFrom":subQ1}),-1.0]])]});}
            var Q53;
            {var subQ0=sQuery(id+"F0.wireOp",EDGE,"E29");var subQ1=sQuery(id+"F0.wireOp",EDGE,"E17.right");var subQ2=makeQuery(id+"F0.imprint","INTERSECT",VERTEX,{"derivedFrom":[subQ1,subQ0]});Q53=makeQuery(id+"F0.imprint","IMPRINT",FACE,{"disambiguationData":[TD([[makeQuery(id+"F0.imprint","IMPRINT",EDGE,{"disambiguationData":[TD([[subQ2,-1.0]])],"derivedFrom":subQ1}),-1.0]])]});}
            var Q54;
            {var subQ0=sQuery(id+"F0.wireOp",EDGE,"E28");var subQ1=sQuery(id+"F0.wireOp",EDGE,"E16.right");var subQ2=makeQuery(id+"F0.imprint","INTERSECT",VERTEX,{"derivedFrom":[subQ1,subQ0]});Q54=makeQuery(id+"F0.imprint","IMPRINT",FACE,{"disambiguationData":[TD([[makeQuery(id+"F0.imprint","IMPRINT",EDGE,{"disambiguationData":[TD([[subQ2,-1.0]])],"derivedFrom":subQ1}),-1.0]])]});}
            var Q55;
            {var subQ0=sQuery(id+"F0.wireOp",EDGE,"E27");var subQ1=sQuery(id+"F0.wireOp",EDGE,"E15.right");var subQ2=makeQuery(id+"F0.imprint","INTERSECT",VERTEX,{"derivedFrom":[subQ1,subQ0]});Q55=makeQuery(id+"F0.imprint","IMPRINT",FACE,{"disambiguationData":[TD([[makeQuery(id+"F0.imprint","IMPRINT",EDGE,{"disambiguationData":[TD([[subQ2,-1.0]])],"derivedFrom":subQ1}),-1.0]])]});}
            var Q56;
            {var subQ0=sQuery(id+"F0.wireOp",EDGE,"E25");var subQ1=sQuery(id+"F0.wireOp",EDGE,"E13.right");var subQ2=makeQuery(id+"F0.imprint","INTERSECT",VERTEX,{"derivedFrom":[subQ1,subQ0]});Q56=makeQuery(id+"F0.imprint","IMPRINT",FACE,{"disambiguationData":[TD([[makeQuery(id+"F0.imprint","IMPRINT",EDGE,{"disambiguationData":[TD([[subQ2,-1.0]])],"derivedFrom":subQ1}),-1.0]])]});}
            var Q57;
            {var subQ0=sQuery(id+"F0.wireOp",EDGE,"E24");var subQ1=sQuery(id+"F0.wireOp",EDGE,"E12.right");var subQ2=makeQuery(id+"F0.imprint","INTERSECT",VERTEX,{"derivedFrom":[subQ1,subQ0]});Q57=makeQuery(id+"F0.imprint","IMPRINT",FACE,{"disambiguationData":[TD([[makeQuery(id+"F0.imprint","IMPRINT",EDGE,{"disambiguationData":[TD([[subQ2,-1.0]])],"derivedFrom":subQ1}),-1.0]])]});}
            var Q58;
            {var subQ0=sQuery(id+"F0.wireOp",EDGE,"E26");var subQ1=sQuery(id+"F0.wireOp",EDGE,"E14.right");var subQ2=makeQuery(id+"F0.imprint","INTERSECT",VERTEX,{"derivedFrom":[subQ1,subQ0]});Q58=makeQuery(id+"F0.imprint","IMPRINT",FACE,{"disambiguationData":[TD([[makeQuery(id+"F0.imprint","IMPRINT",EDGE,{"disambiguationData":[TD([[subQ2,-1.0]])],"derivedFrom":subQ1}),-1.0]])]});}
            var Q59;
            {var subQ0=sQuery(id+"F0.wireOp",EDGE,"E12.right");var subQ1=sQuery(id+"F0.wireOp",EDGE,"E8.top");var subQ2=makeQuery(id+"F0.imprint","INTERSECT",VERTEX,{"derivedFrom":[subQ1,subQ0]});Q59=makeQuery(id+"F0.imprint","IMPRINT",FACE,{"disambiguationData":[TD([[makeQuery(id+"F0.imprint","IMPRINT",EDGE,{"disambiguationData":[TD([[subQ2,-1.0]])],"derivedFrom":subQ1}),-1.0]])]});}
            var Q60;
            {var subQ0=sQuery(id+"F0.wireOp",EDGE,"E14.right");var subQ1=sQuery(id+"F0.wireOp",EDGE,"E8.top");var subQ2=makeQuery(id+"F0.imprint","INTERSECT",VERTEX,{"derivedFrom":[subQ1,subQ0]});Q60=makeQuery(id+"F0.imprint","IMPRINT",FACE,{"disambiguationData":[TD([[makeQuery(id+"F0.imprint","IMPRINT",EDGE,{"disambiguationData":[TD([[subQ2,-1.0]])],"derivedFrom":subQ1}),-1.0]])]});}
            var Q61;
            {var subQ0=sQuery(id+"F0.wireOp",EDGE,"E24");var subQ1=sQuery(id+"F0.wireOp",EDGE,"E14.right");var subQ2=makeQuery(id+"F0.imprint","INTERSECT",VERTEX,{"derivedFrom":[subQ1,subQ0]});Q61=makeQuery(id+"F0.imprint","IMPRINT",FACE,{"disambiguationData":[TD([[makeQuery(id+"F0.imprint","IMPRINT",EDGE,{"disambiguationData":[TD([[subQ2,-1.0]])],"derivedFrom":subQ1}),-1.0]])]});}
            var Q62;
            {var subQ0=sQuery(id+"F0.wireOp",EDGE,"E25");var subQ1=sQuery(id+"F0.wireOp",EDGE,"E15.right");var subQ2=makeQuery(id+"F0.imprint","INTERSECT",VERTEX,{"derivedFrom":[subQ1,subQ0]});Q62=makeQuery(id+"F0.imprint","IMPRINT",FACE,{"disambiguationData":[TD([[makeQuery(id+"F0.imprint","IMPRINT",EDGE,{"disambiguationData":[TD([[subQ2,-1.0]])],"derivedFrom":subQ1}),-1.0]])]});}
            var Q63;
            {var subQ0=sQuery(id+"F0.wireOp",EDGE,"E26");var subQ1=sQuery(id+"F0.wireOp",EDGE,"E16.right");var subQ2=makeQuery(id+"F0.imprint","INTERSECT",VERTEX,{"derivedFrom":[subQ1,subQ0]});Q63=makeQuery(id+"F0.imprint","IMPRINT",FACE,{"disambiguationData":[TD([[makeQuery(id+"F0.imprint","IMPRINT",EDGE,{"disambiguationData":[TD([[subQ2,-1.0]])],"derivedFrom":subQ1}),-1.0]])]});}
            var Q64;
            {var subQ0=sQuery(id+"F0.wireOp",EDGE,"E27");var subQ1=sQuery(id+"F0.wireOp",EDGE,"E17.right");var subQ2=makeQuery(id+"F0.imprint","INTERSECT",VERTEX,{"derivedFrom":[subQ1,subQ0]});Q64=makeQuery(id+"F0.imprint","IMPRINT",FACE,{"disambiguationData":[TD([[makeQuery(id+"F0.imprint","IMPRINT",EDGE,{"disambiguationData":[TD([[subQ2,-1.0]])],"derivedFrom":subQ1}),-1.0]])]});}
            var Q65;
            {var subQ0=sQuery(id+"F0.wireOp",EDGE,"E28");var subQ1=sQuery(id+"F0.wireOp",EDGE,"E18.right");var subQ2=makeQuery(id+"F0.imprint","INTERSECT",VERTEX,{"derivedFrom":[subQ1,subQ0]});Q65=makeQuery(id+"F0.imprint","IMPRINT",FACE,{"disambiguationData":[TD([[makeQuery(id+"F0.imprint","IMPRINT",EDGE,{"disambiguationData":[TD([[subQ2,-1.0]])],"derivedFrom":subQ1}),-1.0]])]});}
            var Q66;
            {var subQ0=sQuery(id+"F0.wireOp",EDGE,"E29");var subQ1=sQuery(id+"F0.wireOp",EDGE,"E21.right");var subQ2=makeQuery(id+"F0.imprint","INTERSECT",VERTEX,{"derivedFrom":[subQ1,subQ0]});Q66=makeQuery(id+"F0.imprint","IMPRINT",FACE,{"disambiguationData":[TD([[makeQuery(id+"F0.imprint","IMPRINT",EDGE,{"disambiguationData":[TD([[subQ2,-1.0]])],"derivedFrom":subQ1}),-1.0]])]});}
            var Q67;
            {var subQ0=sQuery(id+"F0.wireOp",EDGE,"E28");var subQ1=sQuery(id+"F0.wireOp",EDGE,"E20.right");var subQ2=makeQuery(id+"F0.imprint","INTERSECT",VERTEX,{"derivedFrom":[subQ1,subQ0]});Q67=makeQuery(id+"F0.imprint","IMPRINT",FACE,{"disambiguationData":[TD([[makeQuery(id+"F0.imprint","IMPRINT",EDGE,{"disambiguationData":[TD([[subQ2,-1.0]])],"derivedFrom":subQ1}),-1.0]])]});}
            var Q68;
            {var subQ0=sQuery(id+"F0.wireOp",EDGE,"E27");var subQ1=sQuery(id+"F0.wireOp",EDGE,"E19.right");var subQ2=makeQuery(id+"F0.imprint","INTERSECT",VERTEX,{"derivedFrom":[subQ1,subQ0]});Q68=makeQuery(id+"F0.imprint","IMPRINT",FACE,{"disambiguationData":[TD([[makeQuery(id+"F0.imprint","IMPRINT",EDGE,{"disambiguationData":[TD([[subQ2,-1.0]])],"derivedFrom":subQ1}),-1.0]])]});}
            var Q69;
            {var subQ0=sQuery(id+"F0.wireOp",EDGE,"E25");var subQ1=sQuery(id+"F0.wireOp",EDGE,"E17.right");var subQ2=makeQuery(id+"F0.imprint","INTERSECT",VERTEX,{"derivedFrom":[subQ1,subQ0]});Q69=makeQuery(id+"F0.imprint","IMPRINT",FACE,{"disambiguationData":[TD([[makeQuery(id+"F0.imprint","IMPRINT",EDGE,{"disambiguationData":[TD([[subQ2,-1.0]])],"derivedFrom":subQ1}),-1.0]])]});}
            var Q70;
            {var subQ0=sQuery(id+"F0.wireOp",EDGE,"E24");var subQ1=sQuery(id+"F0.wireOp",EDGE,"E16.right");var subQ2=makeQuery(id+"F0.imprint","INTERSECT",VERTEX,{"derivedFrom":[subQ1,subQ0]});Q70=makeQuery(id+"F0.imprint","IMPRINT",FACE,{"disambiguationData":[TD([[makeQuery(id+"F0.imprint","IMPRINT",EDGE,{"disambiguationData":[TD([[subQ2,-1.0]])],"derivedFrom":subQ1}),-1.0]])]});}
            var Q71;
            {var subQ0=sQuery(id+"F0.wireOp",EDGE,"E16.right");var subQ1=sQuery(id+"F0.wireOp",EDGE,"E8.top");var subQ2=makeQuery(id+"F0.imprint","INTERSECT",VERTEX,{"derivedFrom":[subQ1,subQ0]});Q71=makeQuery(id+"F0.imprint","IMPRINT",FACE,{"disambiguationData":[TD([[makeQuery(id+"F0.imprint","IMPRINT",EDGE,{"disambiguationData":[TD([[subQ2,-1.0]])],"derivedFrom":subQ1}),-1.0]])]});}
            var Q72;
            {var subQ0=sQuery(id+"F0.wireOp",EDGE,"E26");var subQ1=sQuery(id+"F0.wireOp",EDGE,"E18.right");var subQ2=makeQuery(id+"F0.imprint","INTERSECT",VERTEX,{"derivedFrom":[subQ1,subQ0]});Q72=makeQuery(id+"F0.imprint","IMPRINT",FACE,{"disambiguationData":[TD([[makeQuery(id+"F0.imprint","IMPRINT",EDGE,{"disambiguationData":[TD([[subQ2,-1.0]])],"derivedFrom":subQ1}),-1.0]])]});}
            var Q73;
            {var subQ0=sQuery(id+"F0.wireOp",EDGE,"E18.right");var subQ1=sQuery(id+"F0.wireOp",EDGE,"E8.top");var subQ2=makeQuery(id+"F0.imprint","INTERSECT",VERTEX,{"derivedFrom":[subQ1,subQ0]});Q73=makeQuery(id+"F0.imprint","IMPRINT",FACE,{"disambiguationData":[TD([[makeQuery(id+"F0.imprint","IMPRINT",EDGE,{"disambiguationData":[TD([[subQ2,-1.0]])],"derivedFrom":subQ1}),-1.0]])]});}
            var Q74;
            {var subQ0=sQuery(id+"F0.wireOp",EDGE,"E24");var subQ1=sQuery(id+"F0.wireOp",EDGE,"E18.right");var subQ2=makeQuery(id+"F0.imprint","INTERSECT",VERTEX,{"derivedFrom":[subQ1,subQ0]});Q74=makeQuery(id+"F0.imprint","IMPRINT",FACE,{"disambiguationData":[TD([[makeQuery(id+"F0.imprint","IMPRINT",EDGE,{"disambiguationData":[TD([[subQ2,-1.0]])],"derivedFrom":subQ1}),-1.0]])]});}
            var Q75;
            {var subQ0=sQuery(id+"F0.wireOp",EDGE,"E25");var subQ1=sQuery(id+"F0.wireOp",EDGE,"E19.right");var subQ2=makeQuery(id+"F0.imprint","INTERSECT",VERTEX,{"derivedFrom":[subQ1,subQ0]});Q75=makeQuery(id+"F0.imprint","IMPRINT",FACE,{"disambiguationData":[TD([[makeQuery(id+"F0.imprint","IMPRINT",EDGE,{"disambiguationData":[TD([[subQ2,-1.0]])],"derivedFrom":subQ1}),-1.0]])]});}
            var Q76;
            {var subQ0=sQuery(id+"F0.wireOp",EDGE,"E26");var subQ1=sQuery(id+"F0.wireOp",EDGE,"E20.right");var subQ2=makeQuery(id+"F0.imprint","INTERSECT",VERTEX,{"derivedFrom":[subQ1,subQ0]});Q76=makeQuery(id+"F0.imprint","IMPRINT",FACE,{"disambiguationData":[TD([[makeQuery(id+"F0.imprint","IMPRINT",EDGE,{"disambiguationData":[TD([[subQ2,-1.0]])],"derivedFrom":subQ1}),-1.0]])]});}
            var Q77;
            {var subQ0=sQuery(id+"F0.wireOp",EDGE,"E27");var subQ1=sQuery(id+"F0.wireOp",EDGE,"E21.right");var subQ2=makeQuery(id+"F0.imprint","INTERSECT",VERTEX,{"derivedFrom":[subQ1,subQ0]});Q77=makeQuery(id+"F0.imprint","IMPRINT",FACE,{"disambiguationData":[TD([[makeQuery(id+"F0.imprint","IMPRINT",EDGE,{"disambiguationData":[TD([[subQ2,-1.0]])],"derivedFrom":subQ1}),-1.0]])]});}
            var Q78;
            {var subQ0=sQuery(id+"F0.wireOp",EDGE,"E28");var subQ1=sQuery(id+"F0.wireOp",EDGE,"E22.right");var subQ2=makeQuery(id+"F0.imprint","INTERSECT",VERTEX,{"derivedFrom":[subQ1,subQ0]});Q78=makeQuery(id+"F0.imprint","IMPRINT",FACE,{"disambiguationData":[TD([[makeQuery(id+"F0.imprint","IMPRINT",EDGE,{"disambiguationData":[TD([[subQ2,-1.0]])],"derivedFrom":subQ1}),-1.0]])]});}
            var Q79;
            {var subQ1=sQuery(id+"F0.wireOp",EDGE,"E23.right");var subQ3=sQuery(id+"F0.wireOp",EDGE,"E29");var subQ4=makeQuery(id+"F0.imprint","INTERSECT",VERTEX,{"derivedFrom":[subQ1,subQ3]});Q79=makeQuery(id+"F0.imprint","IMPRINT",FACE,{"disambiguationData":[TD([[makeQuery(id+"F0.imprint","IMPRINT",EDGE,{"disambiguationData":[TD([[subQ4,-1.0]])],"derivedFrom":subQ3}),1.0]])]});}
            var Q80;
            {var subQ1=sQuery(id+"F0.wireOp",EDGE,"E2");var subQ5=sQuery(id+"F0.wireOp",EDGE,"E3");var subQ6=makeQuery(id+"F0.imprint","INTERSECT",VERTEX,{"derivedFrom":[subQ1,subQ5]});Q80=makeQuery(id+"F0.imprint","IMPRINT",FACE,{"disambiguationData":[TD([[makeQuery(id+"F0.imprint","IMPRINT",EDGE,{"disambiguationData":[TD([[subQ6,1.0]])],"derivedFrom":subQ1}),1.0]])]});}
            var Q81;
            {var subQ0=sQuery(id+"F0.wireOp",EDGE,"E37");var subQ1=sQuery(id+"F0.wireOp",EDGE,"E2");var subQ2=makeQuery(id+"F0.imprint","INTERSECT",VERTEX,{"derivedFrom":[subQ1,subQ0]});Q81=makeQuery(id+"F0.imprint","IMPRINT",FACE,{"disambiguationData":[TD([[makeQuery(id+"F0.imprint","IMPRINT",EDGE,{"disambiguationData":[TD([[subQ2,1.0]])],"derivedFrom":subQ1}),1.0]])]});}
            var Q82;
            {var subQ0=sQuery(id+"F0.wireOp",EDGE,"E38");var subQ1=sQuery(id+"F0.wireOp",EDGE,"E28");var subQ2=makeQuery(id+"F0.imprint","INTERSECT",VERTEX,{"derivedFrom":[subQ1,subQ0]});Q82=makeQuery(id+"F0.imprint","IMPRINT",FACE,{"disambiguationData":[TD([[makeQuery(id+"F0.imprint","IMPRINT",EDGE,{"disambiguationData":[TD([[subQ2,-1.0]])],"derivedFrom":subQ1}),-1.0]])]});}
            var Q83;
            {var subQ0=sQuery(id+"F0.wireOp",EDGE,"E38");var subQ1=sQuery(id+"F0.wireOp",EDGE,"E29");var subQ2=makeQuery(id+"F0.imprint","INTERSECT",VERTEX,{"derivedFrom":[subQ1,subQ0]});Q83=makeQuery(id+"F0.imprint","IMPRINT",FACE,{"disambiguationData":[TD([[makeQuery(id+"F0.imprint","IMPRINT",EDGE,{"disambiguationData":[TD([[subQ2,-1.0]])],"derivedFrom":subQ1}),1.0]])]});}
            var Q84;
            {var subQ0=sQuery(id+"F0.wireOp",EDGE,"E27");var subQ1=sQuery(id+"F0.wireOp",EDGE,"E23.right");var subQ2=makeQuery(id+"F0.imprint","INTERSECT",VERTEX,{"derivedFrom":[subQ1,subQ0]});Q84=makeQuery(id+"F0.imprint","IMPRINT",FACE,{"disambiguationData":[TD([[makeQuery(id+"F0.imprint","IMPRINT",EDGE,{"disambiguationData":[TD([[subQ2,-1.0]])],"derivedFrom":subQ1}),-1.0]])]});}
            var Q85;
            {var subQ0=sQuery(id+"F0.wireOp",EDGE,"E26");var subQ1=sQuery(id+"F0.wireOp",EDGE,"E22.right");var subQ2=makeQuery(id+"F0.imprint","INTERSECT",VERTEX,{"derivedFrom":[subQ1,subQ0]});Q85=makeQuery(id+"F0.imprint","IMPRINT",FACE,{"disambiguationData":[TD([[makeQuery(id+"F0.imprint","IMPRINT",EDGE,{"disambiguationData":[TD([[subQ2,-1.0]])],"derivedFrom":subQ1}),-1.0]])]});}
            var Q86;
            {var subQ0=sQuery(id+"F0.wireOp",EDGE,"E25");var subQ1=sQuery(id+"F0.wireOp",EDGE,"E21.right");var subQ2=makeQuery(id+"F0.imprint","INTERSECT",VERTEX,{"derivedFrom":[subQ1,subQ0]});Q86=makeQuery(id+"F0.imprint","IMPRINT",FACE,{"disambiguationData":[TD([[makeQuery(id+"F0.imprint","IMPRINT",EDGE,{"disambiguationData":[TD([[subQ2,-1.0]])],"derivedFrom":subQ1}),-1.0]])]});}
            var Q87;
            {var subQ0=sQuery(id+"F0.wireOp",EDGE,"E24");var subQ1=sQuery(id+"F0.wireOp",EDGE,"E20.right");var subQ2=makeQuery(id+"F0.imprint","INTERSECT",VERTEX,{"derivedFrom":[subQ1,subQ0]});Q87=makeQuery(id+"F0.imprint","IMPRINT",FACE,{"disambiguationData":[TD([[makeQuery(id+"F0.imprint","IMPRINT",EDGE,{"disambiguationData":[TD([[subQ2,-1.0]])],"derivedFrom":subQ1}),-1.0]])]});}
            var Q88;
            {var subQ0=sQuery(id+"F0.wireOp",EDGE,"E20.right");var subQ1=sQuery(id+"F0.wireOp",EDGE,"E8.top");var subQ2=makeQuery(id+"F0.imprint","INTERSECT",VERTEX,{"derivedFrom":[subQ1,subQ0]});Q88=makeQuery(id+"F0.imprint","IMPRINT",FACE,{"disambiguationData":[TD([[makeQuery(id+"F0.imprint","IMPRINT",EDGE,{"disambiguationData":[TD([[subQ2,-1.0]])],"derivedFrom":subQ1}),-1.0]])]});}
            var Q89;
            {var subQ0=sQuery(id+"F0.wireOp",EDGE,"E22.right");var subQ1=sQuery(id+"F0.wireOp",EDGE,"E8.top");var subQ2=makeQuery(id+"F0.imprint","INTERSECT",VERTEX,{"derivedFrom":[subQ1,subQ0]});Q89=makeQuery(id+"F0.imprint","IMPRINT",FACE,{"disambiguationData":[TD([[makeQuery(id+"F0.imprint","IMPRINT",EDGE,{"disambiguationData":[TD([[subQ2,-1.0]])],"derivedFrom":subQ1}),-1.0]])]});}
            var Q90;
            {var subQ0=sQuery(id+"F0.wireOp",EDGE,"E24");var subQ1=sQuery(id+"F0.wireOp",EDGE,"E22.right");var subQ2=makeQuery(id+"F0.imprint","INTERSECT",VERTEX,{"derivedFrom":[subQ1,subQ0]});Q90=makeQuery(id+"F0.imprint","IMPRINT",FACE,{"disambiguationData":[TD([[makeQuery(id+"F0.imprint","IMPRINT",EDGE,{"disambiguationData":[TD([[subQ2,-1.0]])],"derivedFrom":subQ1}),-1.0]])]});}
            var Q91;
            {var subQ0=sQuery(id+"F0.wireOp",EDGE,"E25");var subQ1=sQuery(id+"F0.wireOp",EDGE,"E23.right");var subQ2=makeQuery(id+"F0.imprint","INTERSECT",VERTEX,{"derivedFrom":[subQ1,subQ0]});Q91=makeQuery(id+"F0.imprint","IMPRINT",FACE,{"disambiguationData":[TD([[makeQuery(id+"F0.imprint","IMPRINT",EDGE,{"disambiguationData":[TD([[subQ2,-1.0]])],"derivedFrom":subQ1}),-1.0]])]});}
            var Q92;
            {var subQ0=sQuery(id+"F0.wireOp",EDGE,"E38");var subQ1=sQuery(id+"F0.wireOp",EDGE,"E26");var subQ2=makeQuery(id+"F0.imprint","INTERSECT",VERTEX,{"derivedFrom":[subQ1,subQ0]});Q92=makeQuery(id+"F0.imprint","IMPRINT",FACE,{"disambiguationData":[TD([[makeQuery(id+"F0.imprint","IMPRINT",EDGE,{"disambiguationData":[TD([[subQ2,-1.0]])],"derivedFrom":subQ1}),-1.0]])]});}
            var Q93;
            {var subQ0=sQuery(id+"F0.wireOp",EDGE,"E37");var subQ1=sQuery(id+"F0.wireOp",EDGE,"E27");var subQ2=makeQuery(id+"F0.imprint","INTERSECT",VERTEX,{"derivedFrom":[subQ1,subQ0]});Q93=makeQuery(id+"F0.imprint","IMPRINT",FACE,{"disambiguationData":[TD([[makeQuery(id+"F0.imprint","IMPRINT",EDGE,{"disambiguationData":[TD([[subQ2,-1.0]])],"derivedFrom":subQ1}),-1.0]])]});}
            var Q94;
            {var subQ0=sQuery(id+"F0.wireOp",EDGE,"E36");var subQ1=sQuery(id+"F0.wireOp",EDGE,"E28");var subQ2=makeQuery(id+"F0.imprint","INTERSECT",VERTEX,{"derivedFrom":[subQ1,subQ0]});Q94=makeQuery(id+"F0.imprint","IMPRINT",FACE,{"disambiguationData":[TD([[makeQuery(id+"F0.imprint","IMPRINT",EDGE,{"disambiguationData":[TD([[subQ2,-1.0]])],"derivedFrom":subQ1}),-1.0]])]});}
            var Q95;
            {var subQ0=sQuery(id+"F0.wireOp",EDGE,"E36");var subQ1=sQuery(id+"F0.wireOp",EDGE,"E29");var subQ2=makeQuery(id+"F0.imprint","INTERSECT",VERTEX,{"derivedFrom":[subQ1,subQ0]});Q95=makeQuery(id+"F0.imprint","IMPRINT",FACE,{"disambiguationData":[TD([[makeQuery(id+"F0.imprint","IMPRINT",EDGE,{"disambiguationData":[TD([[subQ2,-1.0]])],"derivedFrom":subQ1}),1.0]])]});}
            var Q96;
            {var subQ0=sQuery(id+"F0.wireOp",EDGE,"E34");var subQ1=sQuery(id+"F0.wireOp",EDGE,"E33");var subQ2=makeQuery(id+"F0.imprint","INTERSECT",VERTEX,{"derivedFrom":[subQ1,subQ0]});Q96=makeQuery(id+"F0.imprint","IMPRINT",FACE,{"disambiguationData":[TD([[makeQuery(id+"F0.imprint","IMPRINT",EDGE,{"disambiguationData":[TD([[subQ2,-1.0]])],"derivedFrom":subQ1}),-1.0]])]});}
            var Q97;
            {var subQ0=sQuery(id+"F0.wireOp",EDGE,"E39");var subQ1=sQuery(id+"F0.wireOp",EDGE,"E33");var subQ2=makeQuery(id+"F0.imprint","INTERSECT",VERTEX,{"derivedFrom":[subQ1,subQ0]});Q97=makeQuery(id+"F0.imprint","IMPRINT",FACE,{"disambiguationData":[TD([[makeQuery(id+"F0.imprint","IMPRINT",EDGE,{"disambiguationData":[TD([[subQ2,-1.0]])],"derivedFrom":subQ1}),-1.0]])]});}
            var Q98;
            {var subQ0=sQuery(id+"F0.wireOp",EDGE,"E34");var subQ1=sQuery(id+"F0.wireOp",EDGE,"E29");var subQ2=makeQuery(id+"F0.imprint","INTERSECT",VERTEX,{"derivedFrom":[subQ1,subQ0]});Q98=makeQuery(id+"F0.imprint","IMPRINT",FACE,{"disambiguationData":[TD([[makeQuery(id+"F0.imprint","IMPRINT",EDGE,{"disambiguationData":[TD([[subQ2,-1.0]])],"derivedFrom":subQ1}),1.0]])]});}
            var Q99;
            {var subQ0=sQuery(id+"F0.wireOp",EDGE,"E35");var subQ1=sQuery(id+"F0.wireOp",EDGE,"E27");var subQ2=makeQuery(id+"F0.imprint","INTERSECT",VERTEX,{"derivedFrom":[subQ1,subQ0]});Q99=makeQuery(id+"F0.imprint","IMPRINT",FACE,{"disambiguationData":[TD([[makeQuery(id+"F0.imprint","IMPRINT",EDGE,{"disambiguationData":[TD([[subQ2,-1.0]])],"derivedFrom":subQ1}),-1.0]])]});}
            var Q100;
            {var subQ0=sQuery(id+"F0.wireOp",EDGE,"E36");var subQ1=sQuery(id+"F0.wireOp",EDGE,"E26");var subQ2=makeQuery(id+"F0.imprint","INTERSECT",VERTEX,{"derivedFrom":[subQ1,subQ0]});Q100=makeQuery(id+"F0.imprint","IMPRINT",FACE,{"disambiguationData":[TD([[makeQuery(id+"F0.imprint","IMPRINT",EDGE,{"disambiguationData":[TD([[subQ2,-1.0]])],"derivedFrom":subQ1}),-1.0]])]});}
            var Q101;
            {var subQ0=sQuery(id+"F0.wireOp",EDGE,"E37");var subQ1=sQuery(id+"F0.wireOp",EDGE,"E25");var subQ2=makeQuery(id+"F0.imprint","INTERSECT",VERTEX,{"derivedFrom":[subQ1,subQ0]});Q101=makeQuery(id+"F0.imprint","IMPRINT",FACE,{"disambiguationData":[TD([[makeQuery(id+"F0.imprint","IMPRINT",EDGE,{"disambiguationData":[TD([[subQ2,-1.0]])],"derivedFrom":subQ1}),-1.0]])]});}
            var Q102;
            {var subQ0=sQuery(id+"F0.wireOp",EDGE,"E38");var subQ1=sQuery(id+"F0.wireOp",EDGE,"E24");var subQ2=makeQuery(id+"F0.imprint","INTERSECT",VERTEX,{"derivedFrom":[subQ1,subQ0]});Q102=makeQuery(id+"F0.imprint","IMPRINT",FACE,{"disambiguationData":[TD([[makeQuery(id+"F0.imprint","IMPRINT",EDGE,{"disambiguationData":[TD([[subQ2,-1.0]])],"derivedFrom":subQ1}),-1.0]])]});}
            var Q103;
            {var subQ0=sQuery(id+"F0.wireOp",EDGE,"E45");var subQ1=sQuery(id+"F0.wireOp",EDGE,"E8.top");var subQ2=makeQuery(id+"F0.imprint","INTERSECT",VERTEX,{"derivedFrom":[subQ1,subQ0]});Q103=makeQuery(id+"F0.imprint","IMPRINT",FACE,{"disambiguationData":[TD([[makeQuery(id+"F0.imprint","IMPRINT",EDGE,{"disambiguationData":[TD([[subQ2,-1.0]])],"derivedFrom":subQ1}),-1.0]])]});}
            var Q104;
            {var subQ0=sQuery(id+"F0.wireOp",EDGE,"E34");var subQ1=sQuery(id+"F0.wireOp",EDGE,"E28");var subQ2=makeQuery(id+"F0.imprint","INTERSECT",VERTEX,{"derivedFrom":[subQ1,subQ0]});Q104=makeQuery(id+"F0.imprint","IMPRINT",FACE,{"disambiguationData":[TD([[makeQuery(id+"F0.imprint","IMPRINT",EDGE,{"disambiguationData":[TD([[subQ2,-1.0]])],"derivedFrom":subQ1}),-1.0]])]});}
            var Q105;
            {var subQ0=sQuery(id+"F0.wireOp",EDGE,"E37");var subQ1=sQuery(id+"F0.wireOp",EDGE,"E8.top");var subQ2=makeQuery(id+"F0.imprint","INTERSECT",VERTEX,{"derivedFrom":[subQ1,subQ0]});Q105=makeQuery(id+"F0.imprint","IMPRINT",FACE,{"disambiguationData":[TD([[makeQuery(id+"F0.imprint","IMPRINT",EDGE,{"disambiguationData":[TD([[subQ2,-1.0]])],"derivedFrom":subQ1}),-1.0]])]});}
            var Q106;
            {var subQ0=sQuery(id+"F0.wireOp",EDGE,"E35");var subQ1=sQuery(id+"F0.wireOp",EDGE,"E8.top");var subQ2=makeQuery(id+"F0.imprint","INTERSECT",VERTEX,{"derivedFrom":[subQ1,subQ0]});Q106=makeQuery(id+"F0.imprint","IMPRINT",FACE,{"disambiguationData":[TD([[makeQuery(id+"F0.imprint","IMPRINT",EDGE,{"disambiguationData":[TD([[subQ2,-1.0]])],"derivedFrom":subQ1}),-1.0]])]});}
            var Q107;
            {var subQ0=sQuery(id+"F0.wireOp",EDGE,"E40");var subQ1=sQuery(id+"F0.wireOp",EDGE,"E8.top");var subQ2=makeQuery(id+"F0.imprint","INTERSECT",VERTEX,{"derivedFrom":[subQ1,subQ0]});Q107=makeQuery(id+"F0.imprint","IMPRINT",FACE,{"disambiguationData":[TD([[makeQuery(id+"F0.imprint","IMPRINT",EDGE,{"disambiguationData":[TD([[subQ2,-1.0]])],"derivedFrom":subQ1}),-1.0]])]});}
            var Q108;
            {var subQ0=sQuery(id+"F0.wireOp",EDGE,"E41");var subQ1=sQuery(id+"F0.wireOp",EDGE,"E8.top");var subQ2=makeQuery(id+"F0.imprint","INTERSECT",VERTEX,{"derivedFrom":[subQ1,subQ0]});Q108=makeQuery(id+"F0.imprint","IMPRINT",FACE,{"disambiguationData":[TD([[makeQuery(id+"F0.imprint","IMPRINT",EDGE,{"disambiguationData":[TD([[subQ2,-1.0]])],"derivedFrom":subQ1}),-1.0]])]});}
            var Q109;
            {var subQ0=sQuery(id+"F0.wireOp",EDGE,"E34");var subQ1=sQuery(id+"F0.wireOp",EDGE,"E24");var subQ2=makeQuery(id+"F0.imprint","INTERSECT",VERTEX,{"derivedFrom":[subQ1,subQ0]});Q109=makeQuery(id+"F0.imprint","IMPRINT",FACE,{"disambiguationData":[TD([[makeQuery(id+"F0.imprint","IMPRINT",EDGE,{"disambiguationData":[TD([[subQ2,-1.0]])],"derivedFrom":subQ1}),-1.0]])]});}
            var Q110;
            {var subQ0=sQuery(id+"F0.wireOp",EDGE,"E36");var subQ1=sQuery(id+"F0.wireOp",EDGE,"E24");var subQ2=makeQuery(id+"F0.imprint","INTERSECT",VERTEX,{"derivedFrom":[subQ1,subQ0]});Q110=makeQuery(id+"F0.imprint","IMPRINT",FACE,{"disambiguationData":[TD([[makeQuery(id+"F0.imprint","IMPRINT",EDGE,{"disambiguationData":[TD([[subQ2,-1.0]])],"derivedFrom":subQ1}),-1.0]])]});}
            var Q111;
            {var subQ0=sQuery(id+"F0.wireOp",EDGE,"E39");var subQ1=sQuery(id+"F0.wireOp",EDGE,"E24");var subQ2=makeQuery(id+"F0.imprint","INTERSECT",VERTEX,{"derivedFrom":[subQ1,subQ0]});Q111=makeQuery(id+"F0.imprint","IMPRINT",FACE,{"disambiguationData":[TD([[makeQuery(id+"F0.imprint","IMPRINT",EDGE,{"disambiguationData":[TD([[subQ2,-1.0]])],"derivedFrom":subQ1}),-1.0]])]});}
            var Q112;
            {var subQ0=sQuery(id+"F0.wireOp",EDGE,"E40");var subQ1=sQuery(id+"F0.wireOp",EDGE,"E25");var subQ2=makeQuery(id+"F0.imprint","INTERSECT",VERTEX,{"derivedFrom":[subQ1,subQ0]});Q112=makeQuery(id+"F0.imprint","IMPRINT",FACE,{"disambiguationData":[TD([[makeQuery(id+"F0.imprint","IMPRINT",EDGE,{"disambiguationData":[TD([[subQ2,-1.0]])],"derivedFrom":subQ1}),-1.0]])]});}
            var Q113;
            {var subQ0=sQuery(id+"F0.wireOp",EDGE,"E35");var subQ1=sQuery(id+"F0.wireOp",EDGE,"E25");var subQ2=makeQuery(id+"F0.imprint","INTERSECT",VERTEX,{"derivedFrom":[subQ1,subQ0]});Q113=makeQuery(id+"F0.imprint","IMPRINT",FACE,{"disambiguationData":[TD([[makeQuery(id+"F0.imprint","IMPRINT",EDGE,{"disambiguationData":[TD([[subQ2,-1.0]])],"derivedFrom":subQ1}),-1.0]])]});}
            var Q114;
            {var subQ0=sQuery(id+"F0.wireOp",EDGE,"E41");var subQ1=sQuery(id+"F0.wireOp",EDGE,"E25");var subQ2=makeQuery(id+"F0.imprint","INTERSECT",VERTEX,{"derivedFrom":[subQ1,subQ0]});Q114=makeQuery(id+"F0.imprint","IMPRINT",FACE,{"disambiguationData":[TD([[makeQuery(id+"F0.imprint","IMPRINT",EDGE,{"disambiguationData":[TD([[subQ2,-1.0]])],"derivedFrom":subQ1}),-1.0]])]});}
            var Q115;
            {var subQ0=sQuery(id+"F0.wireOp",EDGE,"E34");var subQ1=sQuery(id+"F0.wireOp",EDGE,"E26");var subQ2=makeQuery(id+"F0.imprint","INTERSECT",VERTEX,{"derivedFrom":[subQ1,subQ0]});Q115=makeQuery(id+"F0.imprint","IMPRINT",FACE,{"disambiguationData":[TD([[makeQuery(id+"F0.imprint","IMPRINT",EDGE,{"disambiguationData":[TD([[subQ2,-1.0]])],"derivedFrom":subQ1}),-1.0]])]});}
            var Q116;
            {var subQ0=sQuery(id+"F0.wireOp",EDGE,"E40");var subQ1=sQuery(id+"F0.wireOp",EDGE,"E27");var subQ2=makeQuery(id+"F0.imprint","INTERSECT",VERTEX,{"derivedFrom":[subQ1,subQ0]});Q116=makeQuery(id+"F0.imprint","IMPRINT",FACE,{"disambiguationData":[TD([[makeQuery(id+"F0.imprint","IMPRINT",EDGE,{"disambiguationData":[TD([[subQ2,-1.0]])],"derivedFrom":subQ1}),-1.0]])]});}
            var Q117;
            {var subQ0=sQuery(id+"F0.wireOp",EDGE,"E39");var subQ1=sQuery(id+"F0.wireOp",EDGE,"E26");var subQ2=makeQuery(id+"F0.imprint","INTERSECT",VERTEX,{"derivedFrom":[subQ1,subQ0]});Q117=makeQuery(id+"F0.imprint","IMPRINT",FACE,{"disambiguationData":[TD([[makeQuery(id+"F0.imprint","IMPRINT",EDGE,{"disambiguationData":[TD([[subQ2,-1.0]])],"derivedFrom":subQ1}),-1.0]])]});}
            var Q118;
            {var subQ0=sQuery(id+"F0.wireOp",EDGE,"E41");var subQ1=sQuery(id+"F0.wireOp",EDGE,"E27");var subQ2=makeQuery(id+"F0.imprint","INTERSECT",VERTEX,{"derivedFrom":[subQ1,subQ0]});Q118=makeQuery(id+"F0.imprint","IMPRINT",FACE,{"disambiguationData":[TD([[makeQuery(id+"F0.imprint","IMPRINT",EDGE,{"disambiguationData":[TD([[subQ2,-1.0]])],"derivedFrom":subQ1}),-1.0]])]});}
            var Q119;
            {var subQ0=sQuery(id+"F0.wireOp",EDGE,"E39");var subQ1=sQuery(id+"F0.wireOp",EDGE,"E28");var subQ2=makeQuery(id+"F0.imprint","INTERSECT",VERTEX,{"derivedFrom":[subQ1,subQ0]});Q119=makeQuery(id+"F0.imprint","IMPRINT",FACE,{"disambiguationData":[TD([[makeQuery(id+"F0.imprint","IMPRINT",EDGE,{"disambiguationData":[TD([[subQ2,-1.0]])],"derivedFrom":subQ1}),-1.0]])]});}
            var Q120;
            {var subQ0=sQuery(id+"F0.wireOp",EDGE,"E39");var subQ1=sQuery(id+"F0.wireOp",EDGE,"E29");var subQ2=makeQuery(id+"F0.imprint","INTERSECT",VERTEX,{"derivedFrom":[subQ1,subQ0]});Q120=makeQuery(id+"F0.imprint","IMPRINT",FACE,{"disambiguationData":[TD([[makeQuery(id+"F0.imprint","IMPRINT",EDGE,{"disambiguationData":[TD([[subQ2,-1.0]])],"derivedFrom":subQ1}),1.0]])]});}
            var Q121;
            {var subQ0=sQuery(id+"F0.wireOp",EDGE,"E34");var subQ1=sQuery(id+"F0.wireOp",EDGE,"E1");var subQ2=makeQuery(id+"F0.imprint","INTERSECT",VERTEX,{"derivedFrom":[subQ1,subQ0]});Q121=makeQuery(id+"F0.imprint","IMPRINT",FACE,{"disambiguationData":[TD([[makeQuery(id+"F0.imprint","IMPRINT",EDGE,{"disambiguationData":[TD([[subQ2,1.0]])],"derivedFrom":subQ1}),1.0]])]});}
            var Q122;
            {var subQ1=sQuery(id+"F0.wireOp",EDGE,"E2");var subQ6=sQuery(id+"F0.wireOp",EDGE,"E1");var subQ9=makeQuery(id+"F0.imprint","INTERSECT",VERTEX,{"derivedFrom":[subQ6,subQ1]});Q122=makeQuery(id+"F0.imprint","IMPRINT",FACE,{"disambiguationData":[TD([[makeQuery(id+"F0.imprint","IMPRINT",EDGE,{"disambiguationData":[TD([[subQ9,1.0]])],"derivedFrom":subQ6}),1.0]])]});}
            var Q123;
            {var subQ0=sQuery(id+"F0.wireOp",EDGE,"E39");var subQ1=sQuery(id+"F0.wireOp",EDGE,"E1");var subQ2=makeQuery(id+"F0.imprint","INTERSECT",VERTEX,{"derivedFrom":[subQ1,subQ0]});Q123=makeQuery(id+"F0.imprint","IMPRINT",FACE,{"disambiguationData":[TD([[makeQuery(id+"F0.imprint","IMPRINT",EDGE,{"disambiguationData":[TD([[subQ2,1.0]])],"derivedFrom":subQ1}),1.0]])]});}
            var Q124;
            {var subQ0=sQuery(id+"F0.wireOp",EDGE,"E33");var subQ1=sQuery(id+"F0.wireOp",EDGE,"E0.right");var subQ2=makeQuery(id+"F0.imprint","INTERSECT",VERTEX,{"derivedFrom":[subQ1,subQ0]});Q124=makeQuery(id+"F0.imprint","IMPRINT",FACE,{"disambiguationData":[TD([[makeQuery(id+"F0.imprint","IMPRINT",EDGE,{"disambiguationData":[TD([[subQ2,1.0]])],"derivedFrom":subQ1}),-1.0]])]});}
            var Q125;
            {var subQ0=sQuery(id+"F0.wireOp",EDGE,"E28");var subQ1=sQuery(id+"F0.wireOp",EDGE,"E0.right");var subQ2=makeQuery(id+"F0.imprint","INTERSECT",VERTEX,{"derivedFrom":[subQ1,subQ0]});Q125=makeQuery(id+"F0.imprint","IMPRINT",FACE,{"disambiguationData":[TD([[makeQuery(id+"F0.imprint","IMPRINT",EDGE,{"disambiguationData":[TD([[subQ2,1.0]])],"derivedFrom":subQ1}),-1.0]])]});}
            var Q126;
            {var subQ0=sQuery(id+"F0.wireOp",EDGE,"E26");var subQ1=sQuery(id+"F0.wireOp",EDGE,"E0.right");var subQ2=makeQuery(id+"F0.imprint","INTERSECT",VERTEX,{"derivedFrom":[subQ1,subQ0]});Q126=makeQuery(id+"F0.imprint","IMPRINT",FACE,{"disambiguationData":[TD([[makeQuery(id+"F0.imprint","IMPRINT",EDGE,{"disambiguationData":[TD([[subQ2,1.0]])],"derivedFrom":subQ1}),-1.0]])]});}
            var Q127;
            {var subQ0=sQuery(id+"F0.wireOp",EDGE,"E24");var subQ1=sQuery(id+"F0.wireOp",EDGE,"E0.right");var subQ2=makeQuery(id+"F0.imprint","INTERSECT",VERTEX,{"derivedFrom":[subQ1,subQ0]});Q127=makeQuery(id+"F0.imprint","IMPRINT",FACE,{"disambiguationData":[TD([[makeQuery(id+"F0.imprint","IMPRINT",EDGE,{"disambiguationData":[TD([[subQ2,1.0]])],"derivedFrom":subQ1}),-1.0]])]});}
            var Q128;
            {var subQ0=sQuery(id+"F0.wireOp",EDGE,"E8.left");var subQ1=sQuery(id+"F0.wireOp",EDGE,"E8.bottom");var subQ2=makeQuery(id+"F0.imprint","INTERSECT",VERTEX,{"derivedFrom":[subQ1,subQ0]});Q128=makeQuery(id+"F0.imprint","IMPRINT",FACE,{"disambiguationData":[TD([[makeQuery(id+"F0.imprint","IMPRINT",EDGE,{"disambiguationData":[TD([[subQ2,-1.0]])],"derivedFrom":subQ1}),-1.0]])]});}
            var Q129;
            {var subQ0=sQuery(id+"F0.wireOp",EDGE,"E39");var subQ1=sQuery(id+"F0.wireOp",EDGE,"E8.bottom");var subQ2=makeQuery(id+"F0.imprint","INTERSECT",VERTEX,{"derivedFrom":[subQ1,subQ0]});Q129=makeQuery(id+"F0.imprint","IMPRINT",FACE,{"disambiguationData":[TD([[makeQuery(id+"F0.imprint","IMPRINT",EDGE,{"disambiguationData":[TD([[subQ2,-1.0]])],"derivedFrom":subQ1}),-1.0]])]});}
            var Q130;
            {var subQ0=sQuery(id+"F0.wireOp",EDGE,"E34");var subQ1=sQuery(id+"F0.wireOp",EDGE,"E8.bottom");var subQ2=makeQuery(id+"F0.imprint","INTERSECT",VERTEX,{"derivedFrom":[subQ1,subQ0]});Q130=makeQuery(id+"F0.imprint","IMPRINT",FACE,{"disambiguationData":[TD([[makeQuery(id+"F0.imprint","IMPRINT",EDGE,{"disambiguationData":[TD([[subQ2,-1.0]])],"derivedFrom":subQ1}),-1.0]])]});}
            var Q131;
            {var subQ0=sQuery(id+"F0.wireOp",EDGE,"E38");var subQ1=sQuery(id+"F0.wireOp",EDGE,"E8.bottom");var subQ2=makeQuery(id+"F0.imprint","INTERSECT",VERTEX,{"derivedFrom":[subQ1,subQ0]});Q131=makeQuery(id+"F0.imprint","IMPRINT",FACE,{"disambiguationData":[TD([[makeQuery(id+"F0.imprint","IMPRINT",EDGE,{"disambiguationData":[TD([[subQ2,-1.0]])],"derivedFrom":subQ1}),-1.0]])]});}
            var Q132;
            {var subQ0=sQuery(id+"F0.wireOp",EDGE,"E36");var subQ1=sQuery(id+"F0.wireOp",EDGE,"E8.bottom");var subQ2=makeQuery(id+"F0.imprint","INTERSECT",VERTEX,{"derivedFrom":[subQ1,subQ0]});Q132=makeQuery(id+"F0.imprint","IMPRINT",FACE,{"disambiguationData":[TD([[makeQuery(id+"F0.imprint","IMPRINT",EDGE,{"disambiguationData":[TD([[subQ2,-1.0]])],"derivedFrom":subQ1}),-1.0]])]});}
            var Q133;
            {var subQ5=sQuery(id+"F0.wireOp",EDGE,"E23.bottom");Q133=makeQuery(id+"F0.imprint","IMPRINT",FACE,{"disambiguationData":[TD([[makeQuery(id+"F0.imprint","IMPRINT",EDGE,{"derivedFrom":subQ5}),1.0]])]});}
            var Q134;
            {var subQ5=sQuery(id+"F0.wireOp",EDGE,"E21.bottom");Q134=makeQuery(id+"F0.imprint","IMPRINT",FACE,{"disambiguationData":[TD([[makeQuery(id+"F0.imprint","IMPRINT",EDGE,{"derivedFrom":subQ5}),1.0]])]});}
            var Q135;
            {var subQ5=sQuery(id+"F0.wireOp",EDGE,"E19.bottom");Q135=makeQuery(id+"F0.imprint","IMPRINT",FACE,{"disambiguationData":[TD([[makeQuery(id+"F0.imprint","IMPRINT",EDGE,{"derivedFrom":subQ5}),1.0]])]});}
            var Q136;
            {var subQ5=sQuery(id+"F0.wireOp",EDGE,"E17.bottom");Q136=makeQuery(id+"F0.imprint","IMPRINT",FACE,{"disambiguationData":[TD([[makeQuery(id+"F0.imprint","IMPRINT",EDGE,{"derivedFrom":subQ5}),1.0]])]});}
            var Q137;
            {var subQ5=sQuery(id+"F0.wireOp",EDGE,"E15.bottom");Q137=makeQuery(id+"F0.imprint","IMPRINT",FACE,{"disambiguationData":[TD([[makeQuery(id+"F0.imprint","IMPRINT",EDGE,{"derivedFrom":subQ5}),1.0]])]});}
            var Q138;
            {var subQ5=sQuery(id+"F0.wireOp",EDGE,"E13.bottom");Q138=makeQuery(id+"F0.imprint","IMPRINT",FACE,{"disambiguationData":[TD([[makeQuery(id+"F0.imprint","IMPRINT",EDGE,{"derivedFrom":subQ5}),1.0]])]});}
            var Q139;
            {var subQ5=sQuery(id+"F0.wireOp",EDGE,"E11.bottom");Q139=makeQuery(id+"F0.imprint","IMPRINT",FACE,{"disambiguationData":[TD([[makeQuery(id+"F0.imprint","IMPRINT",EDGE,{"derivedFrom":subQ5}),1.0]])]});}
            var Q140;
            {var subQ0=sQuery(id+"F0.wireOp",EDGE,"E14.top");Q140=makeQuery(id+"F0.imprint","IMPRINT",FACE,{"disambiguationData":[TD([[makeQuery(id+"F0.imprint","IMPRINT",EDGE,{"derivedFrom":subQ0}),-1.0]])]});}
            extrude(context, id + "F1", {"entities" : qUnion([Q0, Q1, Q2, Q3, Q4, Q5, Q6, Q7, Q8, Q9, Q10, Q11, Q12, Q13, Q14, Q15, Q16, Q17, Q18, Q19, Q20, Q21, Q22, Q23, Q24, Q25, Q26, Q27, Q28, Q29, Q30, Q31, Q32, Q33, Q34, Q35, Q36, Q37, Q38, Q39, Q40, Q41, Q42, Q43, Q44, Q45, Q46, Q47, Q48, Q49, Q50, Q51, Q52, Q53, Q54, Q55, Q56, Q57, Q58, Q59, Q60, Q61, Q62, Q63, Q64, Q65, Q66, Q67, Q68, Q69, Q70, Q71, Q72, Q73, Q74, Q75, Q76, Q77, Q78, Q79, Q80, Q81, Q82, Q83, Q84, Q85, Q86, Q87, Q88, Q89, Q90, Q91, Q92, Q93, Q94, Q95, Q96, Q97, Q98, Q99, Q100, Q101, Q102, Q103, Q104, Q105, Q106, Q107, Q108, Q109, Q110, Q111, Q112, Q113, Q114, Q115, Q116, Q117, Q118, Q119, Q120, Q121, Q122, Q123, Q124, Q125, Q126, Q127, Q128, Q129, Q130, Q131, Q132, Q133, Q134, Q135, Q136, Q137, Q138, Q139, Q140]), "depth" : 25 * mm});
        }
        {
            var Q0;
            {var subQ0=sQuery(id+"F0.wireOp",EDGE,"E9.top");Q0=makeQuery(id+"F0.imprint","IMPRINT",FACE,{"disambiguationData":[TD([[makeQuery(id+"F0.imprint","IMPRINT",EDGE,{"derivedFrom":subQ0}),-1.0]])]});}
            var Q1;
            {var subQ0=sQuery(id+"F0.wireOp",EDGE,"E31");var subQ1=sQuery(id+"F0.wireOp",EDGE,"E9.right");var subQ2=makeQuery(id+"F0.imprint","INTERSECT",VERTEX,{"derivedFrom":[subQ1,subQ0]});Q1=makeQuery(id+"F0.imprint","IMPRINT",FACE,{"disambiguationData":[TD([[makeQuery(id+"F0.imprint","IMPRINT",EDGE,{"disambiguationData":[TD([[subQ2,-1.0]])],"derivedFrom":subQ1}),-1.0]])]});}
            var Q2;
            {var subQ0=sQuery(id+"F0.wireOp",EDGE,"E11.top");Q2=makeQuery(id+"F0.imprint","IMPRINT",FACE,{"disambiguationData":[TD([[makeQuery(id+"F0.imprint","IMPRINT",EDGE,{"derivedFrom":subQ0}),-1.0]])]});}
            var Q3;
            {var subQ0=sQuery(id+"F0.wireOp",EDGE,"E31");var subQ1=sQuery(id+"F0.wireOp",EDGE,"E9.left");var subQ2=makeQuery(id+"F0.imprint","INTERSECT",VERTEX,{"derivedFrom":[subQ1,subQ0]});Q3=makeQuery(id+"F0.imprint","IMPRINT",FACE,{"disambiguationData":[TD([[makeQuery(id+"F0.imprint","IMPRINT",EDGE,{"disambiguationData":[TD([[subQ2,1.0]])],"derivedFrom":subQ1}),-1.0]])]});}
            var Q4;
            {var subQ0=sQuery(id+"F0.wireOp",EDGE,"E32");var subQ1=sQuery(id+"F0.wireOp",EDGE,"E10.right");var subQ2=makeQuery(id+"F0.imprint","INTERSECT",VERTEX,{"derivedFrom":[subQ1,subQ0]});Q4=makeQuery(id+"F0.imprint","IMPRINT",FACE,{"disambiguationData":[TD([[makeQuery(id+"F0.imprint","IMPRINT",EDGE,{"disambiguationData":[TD([[subQ2,-1.0]])],"derivedFrom":subQ1}),-1.0]])]});}
            var Q5;
            {var subQ0=sQuery(id+"F0.wireOp",EDGE,"E33");var subQ1=sQuery(id+"F0.wireOp",EDGE,"E9.right");var subQ2=makeQuery(id+"F0.imprint","INTERSECT",VERTEX,{"derivedFrom":[subQ1,subQ0]});Q5=makeQuery(id+"F0.imprint","IMPRINT",FACE,{"disambiguationData":[TD([[makeQuery(id+"F0.imprint","IMPRINT",EDGE,{"disambiguationData":[TD([[subQ2,-1.0]])],"derivedFrom":subQ1}),-1.0]])]});}
            var Q6;
            {var subQ0=sQuery(id+"F0.wireOp",EDGE,"E29");var subQ1=sQuery(id+"F0.wireOp",EDGE,"E9.left");var subQ2=makeQuery(id+"F0.imprint","INTERSECT",VERTEX,{"derivedFrom":[subQ1,subQ0]});Q6=makeQuery(id+"F0.imprint","IMPRINT",FACE,{"disambiguationData":[TD([[makeQuery(id+"F0.imprint","IMPRINT",EDGE,{"disambiguationData":[TD([[subQ2,-1.0]])],"derivedFrom":subQ1}),-1.0]])]});}
            var Q7;
            {var subQ0=sQuery(id+"F0.wireOp",EDGE,"E31");var subQ1=sQuery(id+"F0.wireOp",EDGE,"E11.right");var subQ2=makeQuery(id+"F0.imprint","INTERSECT",VERTEX,{"derivedFrom":[subQ1,subQ0]});Q7=makeQuery(id+"F0.imprint","IMPRINT",FACE,{"disambiguationData":[TD([[makeQuery(id+"F0.imprint","IMPRINT",EDGE,{"disambiguationData":[TD([[subQ2,-1.0]])],"derivedFrom":subQ1}),-1.0]])]});}
            var Q8;
            {var subQ0=sQuery(id+"F0.wireOp",EDGE,"E13.top");Q8=makeQuery(id+"F0.imprint","IMPRINT",FACE,{"disambiguationData":[TD([[makeQuery(id+"F0.imprint","IMPRINT",EDGE,{"derivedFrom":subQ0}),-1.0]])]});}
            var Q9;
            {var subQ0=sQuery(id+"F0.wireOp",EDGE,"E32");var subQ1=sQuery(id+"F0.wireOp",EDGE,"E12.right");var subQ2=makeQuery(id+"F0.imprint","INTERSECT",VERTEX,{"derivedFrom":[subQ1,subQ0]});Q9=makeQuery(id+"F0.imprint","IMPRINT",FACE,{"disambiguationData":[TD([[makeQuery(id+"F0.imprint","IMPRINT",EDGE,{"disambiguationData":[TD([[subQ2,-1.0]])],"derivedFrom":subQ1}),-1.0]])]});}
            var Q10;
            {var subQ0=sQuery(id+"F0.wireOp",EDGE,"E33");var subQ1=sQuery(id+"F0.wireOp",EDGE,"E11.right");var subQ2=makeQuery(id+"F0.imprint","INTERSECT",VERTEX,{"derivedFrom":[subQ1,subQ0]});Q10=makeQuery(id+"F0.imprint","IMPRINT",FACE,{"disambiguationData":[TD([[makeQuery(id+"F0.imprint","IMPRINT",EDGE,{"disambiguationData":[TD([[subQ2,-1.0]])],"derivedFrom":subQ1}),-1.0]])]});}
            var Q11;
            {var subQ0=sQuery(id+"F0.wireOp",EDGE,"E28");var subQ1=sQuery(id+"F0.wireOp",EDGE,"E9.right");var subQ2=makeQuery(id+"F0.imprint","INTERSECT",VERTEX,{"derivedFrom":[subQ1,subQ0]});Q11=makeQuery(id+"F0.imprint","IMPRINT",FACE,{"disambiguationData":[TD([[makeQuery(id+"F0.imprint","IMPRINT",EDGE,{"disambiguationData":[TD([[subQ2,-1.0]])],"derivedFrom":subQ1}),-1.0]])]});}
            var Q12;
            {var subQ0=sQuery(id+"F0.wireOp",EDGE,"E29");var subQ1=sQuery(id+"F0.wireOp",EDGE,"E10.right");var subQ2=makeQuery(id+"F0.imprint","INTERSECT",VERTEX,{"derivedFrom":[subQ1,subQ0]});Q12=makeQuery(id+"F0.imprint","IMPRINT",FACE,{"disambiguationData":[TD([[makeQuery(id+"F0.imprint","IMPRINT",EDGE,{"disambiguationData":[TD([[subQ2,-1.0]])],"derivedFrom":subQ1}),-1.0]])]});}
            var Q13;
            {var subQ0=sQuery(id+"F0.wireOp",EDGE,"E27");var subQ1=sQuery(id+"F0.wireOp",EDGE,"E9.left");var subQ2=makeQuery(id+"F0.imprint","INTERSECT",VERTEX,{"derivedFrom":[subQ1,subQ0]});Q13=makeQuery(id+"F0.imprint","IMPRINT",FACE,{"disambiguationData":[TD([[makeQuery(id+"F0.imprint","IMPRINT",EDGE,{"disambiguationData":[TD([[subQ2,-1.0]])],"derivedFrom":subQ1}),-1.0]])]});}
            var Q14;
            {var subQ0=sQuery(id+"F0.wireOp",EDGE,"E25");var subQ1=sQuery(id+"F0.wireOp",EDGE,"E9.left");var subQ2=makeQuery(id+"F0.imprint","INTERSECT",VERTEX,{"derivedFrom":[subQ1,subQ0]});Q14=makeQuery(id+"F0.imprint","IMPRINT",FACE,{"disambiguationData":[TD([[makeQuery(id+"F0.imprint","IMPRINT",EDGE,{"disambiguationData":[TD([[subQ2,-1.0]])],"derivedFrom":subQ1}),-1.0]])]});}
            var Q15;
            {var subQ0=sQuery(id+"F0.wireOp",EDGE,"E26");var subQ1=sQuery(id+"F0.wireOp",EDGE,"E9.right");var subQ2=makeQuery(id+"F0.imprint","INTERSECT",VERTEX,{"derivedFrom":[subQ1,subQ0]});Q15=makeQuery(id+"F0.imprint","IMPRINT",FACE,{"disambiguationData":[TD([[makeQuery(id+"F0.imprint","IMPRINT",EDGE,{"disambiguationData":[TD([[subQ2,-1.0]])],"derivedFrom":subQ1}),-1.0]])]});}
            var Q16;
            {var subQ0=sQuery(id+"F0.wireOp",EDGE,"E27");var subQ1=sQuery(id+"F0.wireOp",EDGE,"E10.right");var subQ2=makeQuery(id+"F0.imprint","INTERSECT",VERTEX,{"derivedFrom":[subQ1,subQ0]});Q16=makeQuery(id+"F0.imprint","IMPRINT",FACE,{"disambiguationData":[TD([[makeQuery(id+"F0.imprint","IMPRINT",EDGE,{"disambiguationData":[TD([[subQ2,-1.0]])],"derivedFrom":subQ1}),-1.0]])]});}
            var Q17;
            {var subQ0=sQuery(id+"F0.wireOp",EDGE,"E28");var subQ1=sQuery(id+"F0.wireOp",EDGE,"E11.right");var subQ2=makeQuery(id+"F0.imprint","INTERSECT",VERTEX,{"derivedFrom":[subQ1,subQ0]});Q17=makeQuery(id+"F0.imprint","IMPRINT",FACE,{"disambiguationData":[TD([[makeQuery(id+"F0.imprint","IMPRINT",EDGE,{"disambiguationData":[TD([[subQ2,-1.0]])],"derivedFrom":subQ1}),-1.0]])]});}
            var Q18;
            {var subQ0=sQuery(id+"F0.wireOp",EDGE,"E29");var subQ1=sQuery(id+"F0.wireOp",EDGE,"E12.right");var subQ2=makeQuery(id+"F0.imprint","INTERSECT",VERTEX,{"derivedFrom":[subQ1,subQ0]});Q18=makeQuery(id+"F0.imprint","IMPRINT",FACE,{"disambiguationData":[TD([[makeQuery(id+"F0.imprint","IMPRINT",EDGE,{"disambiguationData":[TD([[subQ2,-1.0]])],"derivedFrom":subQ1}),-1.0]])]});}
            var Q19;
            {var subQ0=sQuery(id+"F0.wireOp",EDGE,"E33");var subQ1=sQuery(id+"F0.wireOp",EDGE,"E13.right");var subQ2=makeQuery(id+"F0.imprint","INTERSECT",VERTEX,{"derivedFrom":[subQ1,subQ0]});Q19=makeQuery(id+"F0.imprint","IMPRINT",FACE,{"disambiguationData":[TD([[makeQuery(id+"F0.imprint","IMPRINT",EDGE,{"disambiguationData":[TD([[subQ2,-1.0]])],"derivedFrom":subQ1}),-1.0]])]});}
            var Q20;
            {var subQ0=sQuery(id+"F0.wireOp",EDGE,"E32");var subQ1=sQuery(id+"F0.wireOp",EDGE,"E14.right");var subQ2=makeQuery(id+"F0.imprint","INTERSECT",VERTEX,{"derivedFrom":[subQ1,subQ0]});Q20=makeQuery(id+"F0.imprint","IMPRINT",FACE,{"disambiguationData":[TD([[makeQuery(id+"F0.imprint","IMPRINT",EDGE,{"disambiguationData":[TD([[subQ2,-1.0]])],"derivedFrom":subQ1}),-1.0]])]});}
            var Q21;
            {var subQ0=sQuery(id+"F0.wireOp",EDGE,"E31");var subQ1=sQuery(id+"F0.wireOp",EDGE,"E15.right");var subQ2=makeQuery(id+"F0.imprint","INTERSECT",VERTEX,{"derivedFrom":[subQ1,subQ0]});Q21=makeQuery(id+"F0.imprint","IMPRINT",FACE,{"disambiguationData":[TD([[makeQuery(id+"F0.imprint","IMPRINT",EDGE,{"disambiguationData":[TD([[subQ2,-1.0]])],"derivedFrom":subQ1}),-1.0]])]});}
            var Q22;
            {var subQ0=sQuery(id+"F0.wireOp",EDGE,"E15.top");Q22=makeQuery(id+"F0.imprint","IMPRINT",FACE,{"disambiguationData":[TD([[makeQuery(id+"F0.imprint","IMPRINT",EDGE,{"derivedFrom":subQ0}),-1.0]])]});}
            var Q23;
            {var subQ0=sQuery(id+"F0.wireOp",EDGE,"E31");var subQ1=sQuery(id+"F0.wireOp",EDGE,"E13.right");var subQ2=makeQuery(id+"F0.imprint","INTERSECT",VERTEX,{"derivedFrom":[subQ1,subQ0]});Q23=makeQuery(id+"F0.imprint","IMPRINT",FACE,{"disambiguationData":[TD([[makeQuery(id+"F0.imprint","IMPRINT",EDGE,{"disambiguationData":[TD([[subQ2,-1.0]])],"derivedFrom":subQ1}),-1.0]])]});}
            var Q24;
            {var subQ0=sQuery(id+"F0.wireOp",EDGE,"E9.left");var subQ1=sQuery(id+"F0.wireOp",EDGE,"E8.top");var subQ2=makeQuery(id+"F0.imprint","INTERSECT",VERTEX,{"derivedFrom":[subQ1,subQ0]});Q24=makeQuery(id+"F0.imprint","IMPRINT",FACE,{"disambiguationData":[TD([[makeQuery(id+"F0.imprint","IMPRINT",EDGE,{"disambiguationData":[TD([[subQ2,1.0]])],"derivedFrom":subQ1}),-1.0]])]});}
            var Q25;
            {var subQ0=sQuery(id+"F0.wireOp",EDGE,"E24");var subQ1=sQuery(id+"F0.wireOp",EDGE,"E9.right");var subQ2=makeQuery(id+"F0.imprint","INTERSECT",VERTEX,{"derivedFrom":[subQ1,subQ0]});Q25=makeQuery(id+"F0.imprint","IMPRINT",FACE,{"disambiguationData":[TD([[makeQuery(id+"F0.imprint","IMPRINT",EDGE,{"disambiguationData":[TD([[subQ2,-1.0]])],"derivedFrom":subQ1}),-1.0]])]});}
            var Q26;
            {var subQ0=sQuery(id+"F0.wireOp",EDGE,"E25");var subQ1=sQuery(id+"F0.wireOp",EDGE,"E10.right");var subQ2=makeQuery(id+"F0.imprint","INTERSECT",VERTEX,{"derivedFrom":[subQ1,subQ0]});Q26=makeQuery(id+"F0.imprint","IMPRINT",FACE,{"disambiguationData":[TD([[makeQuery(id+"F0.imprint","IMPRINT",EDGE,{"disambiguationData":[TD([[subQ2,-1.0]])],"derivedFrom":subQ1}),-1.0]])]});}
            var Q27;
            {var subQ0=sQuery(id+"F0.wireOp",EDGE,"E26");var subQ1=sQuery(id+"F0.wireOp",EDGE,"E11.right");var subQ2=makeQuery(id+"F0.imprint","INTERSECT",VERTEX,{"derivedFrom":[subQ1,subQ0]});Q27=makeQuery(id+"F0.imprint","IMPRINT",FACE,{"disambiguationData":[TD([[makeQuery(id+"F0.imprint","IMPRINT",EDGE,{"disambiguationData":[TD([[subQ2,-1.0]])],"derivedFrom":subQ1}),-1.0]])]});}
            var Q28;
            {var subQ0=sQuery(id+"F0.wireOp",EDGE,"E27");var subQ1=sQuery(id+"F0.wireOp",EDGE,"E12.right");var subQ2=makeQuery(id+"F0.imprint","INTERSECT",VERTEX,{"derivedFrom":[subQ1,subQ0]});Q28=makeQuery(id+"F0.imprint","IMPRINT",FACE,{"disambiguationData":[TD([[makeQuery(id+"F0.imprint","IMPRINT",EDGE,{"disambiguationData":[TD([[subQ2,-1.0]])],"derivedFrom":subQ1}),-1.0]])]});}
            var Q29;
            {var subQ0=sQuery(id+"F0.wireOp",EDGE,"E28");var subQ1=sQuery(id+"F0.wireOp",EDGE,"E13.right");var subQ2=makeQuery(id+"F0.imprint","INTERSECT",VERTEX,{"derivedFrom":[subQ1,subQ0]});Q29=makeQuery(id+"F0.imprint","IMPRINT",FACE,{"disambiguationData":[TD([[makeQuery(id+"F0.imprint","IMPRINT",EDGE,{"disambiguationData":[TD([[subQ2,-1.0]])],"derivedFrom":subQ1}),-1.0]])]});}
            var Q30;
            {var subQ0=sQuery(id+"F0.wireOp",EDGE,"E29");var subQ1=sQuery(id+"F0.wireOp",EDGE,"E14.right");var subQ2=makeQuery(id+"F0.imprint","INTERSECT",VERTEX,{"derivedFrom":[subQ1,subQ0]});Q30=makeQuery(id+"F0.imprint","IMPRINT",FACE,{"disambiguationData":[TD([[makeQuery(id+"F0.imprint","IMPRINT",EDGE,{"disambiguationData":[TD([[subQ2,-1.0]])],"derivedFrom":subQ1}),-1.0]])]});}
            var Q31;
            {var subQ0=sQuery(id+"F0.wireOp",EDGE,"E33");var subQ1=sQuery(id+"F0.wireOp",EDGE,"E15.right");var subQ2=makeQuery(id+"F0.imprint","INTERSECT",VERTEX,{"derivedFrom":[subQ1,subQ0]});Q31=makeQuery(id+"F0.imprint","IMPRINT",FACE,{"disambiguationData":[TD([[makeQuery(id+"F0.imprint","IMPRINT",EDGE,{"disambiguationData":[TD([[subQ2,-1.0]])],"derivedFrom":subQ1}),-1.0]])]});}
            var Q32;
            {var subQ0=sQuery(id+"F0.wireOp",EDGE,"E31");var subQ1=sQuery(id+"F0.wireOp",EDGE,"E17.right");var subQ2=makeQuery(id+"F0.imprint","INTERSECT",VERTEX,{"derivedFrom":[subQ1,subQ0]});Q32=makeQuery(id+"F0.imprint","IMPRINT",FACE,{"disambiguationData":[TD([[makeQuery(id+"F0.imprint","IMPRINT",EDGE,{"disambiguationData":[TD([[subQ2,-1.0]])],"derivedFrom":subQ1}),-1.0]])]});}
            var Q33;
            {var subQ0=sQuery(id+"F0.wireOp",EDGE,"E19.top");Q33=makeQuery(id+"F0.imprint","IMPRINT",FACE,{"disambiguationData":[TD([[makeQuery(id+"F0.imprint","IMPRINT",EDGE,{"derivedFrom":subQ0}),-1.0]])]});}
            var Q34;
            {var subQ0=sQuery(id+"F0.wireOp",EDGE,"E17.top");Q34=makeQuery(id+"F0.imprint","IMPRINT",FACE,{"disambiguationData":[TD([[makeQuery(id+"F0.imprint","IMPRINT",EDGE,{"derivedFrom":subQ0}),-1.0]])]});}
            var Q35;
            {var subQ0=sQuery(id+"F0.wireOp",EDGE,"E32");var subQ1=sQuery(id+"F0.wireOp",EDGE,"E16.right");var subQ2=makeQuery(id+"F0.imprint","INTERSECT",VERTEX,{"derivedFrom":[subQ1,subQ0]});Q35=makeQuery(id+"F0.imprint","IMPRINT",FACE,{"disambiguationData":[TD([[makeQuery(id+"F0.imprint","IMPRINT",EDGE,{"disambiguationData":[TD([[subQ2,-1.0]])],"derivedFrom":subQ1}),-1.0]])]});}
            var Q36;
            {var subQ0=sQuery(id+"F0.wireOp",EDGE,"E29");var subQ1=sQuery(id+"F0.wireOp",EDGE,"E16.right");var subQ2=makeQuery(id+"F0.imprint","INTERSECT",VERTEX,{"derivedFrom":[subQ1,subQ0]});Q36=makeQuery(id+"F0.imprint","IMPRINT",FACE,{"disambiguationData":[TD([[makeQuery(id+"F0.imprint","IMPRINT",EDGE,{"disambiguationData":[TD([[subQ2,-1.0]])],"derivedFrom":subQ1}),-1.0]])]});}
            var Q37;
            {var subQ0=sQuery(id+"F0.wireOp",EDGE,"E11.right");var subQ1=sQuery(id+"F0.wireOp",EDGE,"E8.top");var subQ2=makeQuery(id+"F0.imprint","INTERSECT",VERTEX,{"derivedFrom":[subQ1,subQ0]});Q37=makeQuery(id+"F0.imprint","IMPRINT",FACE,{"disambiguationData":[TD([[makeQuery(id+"F0.imprint","IMPRINT",EDGE,{"disambiguationData":[TD([[subQ2,-1.0]])],"derivedFrom":subQ1}),-1.0]])]});}
            var Q38;
            {var subQ0=sQuery(id+"F0.wireOp",EDGE,"E24");var subQ1=sQuery(id+"F0.wireOp",EDGE,"E11.right");var subQ2=makeQuery(id+"F0.imprint","INTERSECT",VERTEX,{"derivedFrom":[subQ1,subQ0]});Q38=makeQuery(id+"F0.imprint","IMPRINT",FACE,{"disambiguationData":[TD([[makeQuery(id+"F0.imprint","IMPRINT",EDGE,{"disambiguationData":[TD([[subQ2,-1.0]])],"derivedFrom":subQ1}),-1.0]])]});}
            var Q39;
            {var subQ0=sQuery(id+"F0.wireOp",EDGE,"E27");var subQ1=sQuery(id+"F0.wireOp",EDGE,"E14.right");var subQ2=makeQuery(id+"F0.imprint","INTERSECT",VERTEX,{"derivedFrom":[subQ1,subQ0]});Q39=makeQuery(id+"F0.imprint","IMPRINT",FACE,{"disambiguationData":[TD([[makeQuery(id+"F0.imprint","IMPRINT",EDGE,{"disambiguationData":[TD([[subQ2,-1.0]])],"derivedFrom":subQ1}),-1.0]])]});}
            var Q40;
            {var subQ0=sQuery(id+"F0.wireOp",EDGE,"E26");var subQ1=sQuery(id+"F0.wireOp",EDGE,"E13.right");var subQ2=makeQuery(id+"F0.imprint","INTERSECT",VERTEX,{"derivedFrom":[subQ1,subQ0]});Q40=makeQuery(id+"F0.imprint","IMPRINT",FACE,{"disambiguationData":[TD([[makeQuery(id+"F0.imprint","IMPRINT",EDGE,{"disambiguationData":[TD([[subQ2,-1.0]])],"derivedFrom":subQ1}),-1.0]])]});}
            var Q41;
            {var subQ0=sQuery(id+"F0.wireOp",EDGE,"E25");var subQ1=sQuery(id+"F0.wireOp",EDGE,"E12.right");var subQ2=makeQuery(id+"F0.imprint","INTERSECT",VERTEX,{"derivedFrom":[subQ1,subQ0]});Q41=makeQuery(id+"F0.imprint","IMPRINT",FACE,{"disambiguationData":[TD([[makeQuery(id+"F0.imprint","IMPRINT",EDGE,{"disambiguationData":[TD([[subQ2,-1.0]])],"derivedFrom":subQ1}),-1.0]])]});}
            var Q42;
            {var subQ0=sQuery(id+"F0.wireOp",EDGE,"E28");var subQ1=sQuery(id+"F0.wireOp",EDGE,"E15.right");var subQ2=makeQuery(id+"F0.imprint","INTERSECT",VERTEX,{"derivedFrom":[subQ1,subQ0]});Q42=makeQuery(id+"F0.imprint","IMPRINT",FACE,{"disambiguationData":[TD([[makeQuery(id+"F0.imprint","IMPRINT",EDGE,{"disambiguationData":[TD([[subQ2,-1.0]])],"derivedFrom":subQ1}),-1.0]])]});}
            var Q43;
            {var subQ0=sQuery(id+"F0.wireOp",EDGE,"E33");var subQ1=sQuery(id+"F0.wireOp",EDGE,"E17.right");var subQ2=makeQuery(id+"F0.imprint","INTERSECT",VERTEX,{"derivedFrom":[subQ1,subQ0]});Q43=makeQuery(id+"F0.imprint","IMPRINT",FACE,{"disambiguationData":[TD([[makeQuery(id+"F0.imprint","IMPRINT",EDGE,{"disambiguationData":[TD([[subQ2,-1.0]])],"derivedFrom":subQ1}),-1.0]])]});}
            var Q44;
            {var subQ0=sQuery(id+"F0.wireOp",EDGE,"E32");var subQ1=sQuery(id+"F0.wireOp",EDGE,"E18.right");var subQ2=makeQuery(id+"F0.imprint","INTERSECT",VERTEX,{"derivedFrom":[subQ1,subQ0]});Q44=makeQuery(id+"F0.imprint","IMPRINT",FACE,{"disambiguationData":[TD([[makeQuery(id+"F0.imprint","IMPRINT",EDGE,{"disambiguationData":[TD([[subQ2,-1.0]])],"derivedFrom":subQ1}),-1.0]])]});}
            var Q45;
            {var subQ0=sQuery(id+"F0.wireOp",EDGE,"E31");var subQ1=sQuery(id+"F0.wireOp",EDGE,"E19.right");var subQ2=makeQuery(id+"F0.imprint","INTERSECT",VERTEX,{"derivedFrom":[subQ1,subQ0]});Q45=makeQuery(id+"F0.imprint","IMPRINT",FACE,{"disambiguationData":[TD([[makeQuery(id+"F0.imprint","IMPRINT",EDGE,{"disambiguationData":[TD([[subQ2,-1.0]])],"derivedFrom":subQ1}),-1.0]])]});}
            var Q46;
            {var subQ0=sQuery(id+"F0.wireOp",EDGE,"E21.top");Q46=makeQuery(id+"F0.imprint","IMPRINT",FACE,{"disambiguationData":[TD([[makeQuery(id+"F0.imprint","IMPRINT",EDGE,{"derivedFrom":subQ0}),-1.0]])]});}
            var Q47;
            {var subQ0=sQuery(id+"F0.wireOp",EDGE,"E23.top");Q47=makeQuery(id+"F0.imprint","IMPRINT",FACE,{"disambiguationData":[TD([[makeQuery(id+"F0.imprint","IMPRINT",EDGE,{"derivedFrom":subQ0}),-1.0]])]});}
            var Q48;
            {var subQ0=sQuery(id+"F0.wireOp",EDGE,"E47");var subQ1=sQuery(id+"F0.wireOp",EDGE,"E0.bottom");var subQ2=makeQuery(id+"F0.imprint","INTERSECT",VERTEX,{"derivedFrom":[subQ1,subQ0]});Q48=makeQuery(id+"F0.imprint","IMPRINT",FACE,{"disambiguationData":[TD([[makeQuery(id+"F0.imprint","IMPRINT",EDGE,{"disambiguationData":[TD([[subQ2,-1.0]])],"derivedFrom":subQ1}),-1.0]])]});}
            var Q49;
            {var subQ3=sQuery(id+"F0.wireOp",EDGE,"E49");Q49=makeQuery(id+"F0.imprint","IMPRINT",FACE,{"disambiguationData":[TD([[makeQuery(id+"F0.imprint","IMPRINT",EDGE,{"derivedFrom":subQ3}),-1.0]])]});}
            var Q50;
            {var subQ3=sQuery(id+"F0.wireOp",EDGE,"E31");var subQ5=sQuery(id+"F0.wireOp",EDGE,"E4");var subQ6=makeQuery(id+"F0.imprint","INTERSECT",VERTEX,{"derivedFrom":[subQ5,subQ3]});Q50=makeQuery(id+"F0.imprint","IMPRINT",FACE,{"disambiguationData":[TD([[makeQuery(id+"F0.imprint","IMPRINT",EDGE,{"disambiguationData":[TD([[subQ6,-1.0]])],"derivedFrom":subQ5}),1.0]])]});}
            var Q51;
            {var subQ0=sQuery(id+"F0.wireOp",EDGE,"E31");var subQ1=sQuery(id+"F0.wireOp",EDGE,"E21.right");var subQ2=makeQuery(id+"F0.imprint","INTERSECT",VERTEX,{"derivedFrom":[subQ1,subQ0]});Q51=makeQuery(id+"F0.imprint","IMPRINT",FACE,{"disambiguationData":[TD([[makeQuery(id+"F0.imprint","IMPRINT",EDGE,{"disambiguationData":[TD([[subQ2,-1.0]])],"derivedFrom":subQ1}),-1.0]])]});}
            var Q52;
            {var subQ0=sQuery(id+"F0.wireOp",EDGE,"E42.trimOffspring");var subQ1=sQuery(id+"F0.wireOp",EDGE,"E4");var subQ2=makeQuery(id+"F0.imprint","INTERSECT",VERTEX,{"derivedFrom":[subQ1,subQ0]});Q52=makeQuery(id+"F0.imprint","IMPRINT",FACE,{"disambiguationData":[TD([[makeQuery(id+"F0.imprint","IMPRINT",EDGE,{"disambiguationData":[TD([[subQ2,1.0]])],"derivedFrom":subQ1}),1.0]])]});}
            var Q53;
            {var subQ0=sQuery(id+"F0.wireOp",EDGE,"E32");var subQ1=sQuery(id+"F0.wireOp",EDGE,"E20.right");var subQ2=makeQuery(id+"F0.imprint","INTERSECT",VERTEX,{"derivedFrom":[subQ1,subQ0]});Q53=makeQuery(id+"F0.imprint","IMPRINT",FACE,{"disambiguationData":[TD([[makeQuery(id+"F0.imprint","IMPRINT",EDGE,{"disambiguationData":[TD([[subQ2,-1.0]])],"derivedFrom":subQ1}),-1.0]])]});}
            var Q54;
            {var subQ0=sQuery(id+"F0.wireOp",EDGE,"E33");var subQ1=sQuery(id+"F0.wireOp",EDGE,"E19.right");var subQ2=makeQuery(id+"F0.imprint","INTERSECT",VERTEX,{"derivedFrom":[subQ1,subQ0]});Q54=makeQuery(id+"F0.imprint","IMPRINT",FACE,{"disambiguationData":[TD([[makeQuery(id+"F0.imprint","IMPRINT",EDGE,{"disambiguationData":[TD([[subQ2,-1.0]])],"derivedFrom":subQ1}),-1.0]])]});}
            var Q55;
            {var subQ0=sQuery(id+"F0.wireOp",EDGE,"E33");var subQ1=sQuery(id+"F0.wireOp",EDGE,"E21.right");var subQ2=makeQuery(id+"F0.imprint","INTERSECT",VERTEX,{"derivedFrom":[subQ1,subQ0]});Q55=makeQuery(id+"F0.imprint","IMPRINT",FACE,{"disambiguationData":[TD([[makeQuery(id+"F0.imprint","IMPRINT",EDGE,{"disambiguationData":[TD([[subQ2,-1.0]])],"derivedFrom":subQ1}),-1.0]])]});}
            var Q56;
            {var subQ0=sQuery(id+"F0.wireOp",EDGE,"E29");var subQ1=sQuery(id+"F0.wireOp",EDGE,"E20.right");var subQ2=makeQuery(id+"F0.imprint","INTERSECT",VERTEX,{"derivedFrom":[subQ1,subQ0]});Q56=makeQuery(id+"F0.imprint","IMPRINT",FACE,{"disambiguationData":[TD([[makeQuery(id+"F0.imprint","IMPRINT",EDGE,{"disambiguationData":[TD([[subQ2,-1.0]])],"derivedFrom":subQ1}),-1.0]])]});}
            var Q57;
            {var subQ0=sQuery(id+"F0.wireOp",EDGE,"E29");var subQ1=sQuery(id+"F0.wireOp",EDGE,"E18.right");var subQ2=makeQuery(id+"F0.imprint","INTERSECT",VERTEX,{"derivedFrom":[subQ1,subQ0]});Q57=makeQuery(id+"F0.imprint","IMPRINT",FACE,{"disambiguationData":[TD([[makeQuery(id+"F0.imprint","IMPRINT",EDGE,{"disambiguationData":[TD([[subQ2,-1.0]])],"derivedFrom":subQ1}),-1.0]])]});}
            var Q58;
            {var subQ0=sQuery(id+"F0.wireOp",EDGE,"E28");var subQ1=sQuery(id+"F0.wireOp",EDGE,"E19.right");var subQ2=makeQuery(id+"F0.imprint","INTERSECT",VERTEX,{"derivedFrom":[subQ1,subQ0]});Q58=makeQuery(id+"F0.imprint","IMPRINT",FACE,{"disambiguationData":[TD([[makeQuery(id+"F0.imprint","IMPRINT",EDGE,{"disambiguationData":[TD([[subQ2,-1.0]])],"derivedFrom":subQ1}),-1.0]])]});}
            var Q59;
            {var subQ0=sQuery(id+"F0.wireOp",EDGE,"E27");var subQ1=sQuery(id+"F0.wireOp",EDGE,"E16.right");var subQ2=makeQuery(id+"F0.imprint","INTERSECT",VERTEX,{"derivedFrom":[subQ1,subQ0]});Q59=makeQuery(id+"F0.imprint","IMPRINT",FACE,{"disambiguationData":[TD([[makeQuery(id+"F0.imprint","IMPRINT",EDGE,{"disambiguationData":[TD([[subQ2,-1.0]])],"derivedFrom":subQ1}),-1.0]])]});}
            var Q60;
            {var subQ0=sQuery(id+"F0.wireOp",EDGE,"E27");var subQ1=sQuery(id+"F0.wireOp",EDGE,"E18.right");var subQ2=makeQuery(id+"F0.imprint","INTERSECT",VERTEX,{"derivedFrom":[subQ1,subQ0]});Q60=makeQuery(id+"F0.imprint","IMPRINT",FACE,{"disambiguationData":[TD([[makeQuery(id+"F0.imprint","IMPRINT",EDGE,{"disambiguationData":[TD([[subQ2,-1.0]])],"derivedFrom":subQ1}),-1.0]])]});}
            var Q61;
            {var subQ0=sQuery(id+"F0.wireOp",EDGE,"E26");var subQ1=sQuery(id+"F0.wireOp",EDGE,"E15.right");var subQ2=makeQuery(id+"F0.imprint","INTERSECT",VERTEX,{"derivedFrom":[subQ1,subQ0]});Q61=makeQuery(id+"F0.imprint","IMPRINT",FACE,{"disambiguationData":[TD([[makeQuery(id+"F0.imprint","IMPRINT",EDGE,{"disambiguationData":[TD([[subQ2,-1.0]])],"derivedFrom":subQ1}),-1.0]])]});}
            var Q62;
            {var subQ0=sQuery(id+"F0.wireOp",EDGE,"E28");var subQ1=sQuery(id+"F0.wireOp",EDGE,"E17.right");var subQ2=makeQuery(id+"F0.imprint","INTERSECT",VERTEX,{"derivedFrom":[subQ1,subQ0]});Q62=makeQuery(id+"F0.imprint","IMPRINT",FACE,{"disambiguationData":[TD([[makeQuery(id+"F0.imprint","IMPRINT",EDGE,{"disambiguationData":[TD([[subQ2,-1.0]])],"derivedFrom":subQ1}),-1.0]])]});}
            var Q63;
            {var subQ0=sQuery(id+"F0.wireOp",EDGE,"E25");var subQ1=sQuery(id+"F0.wireOp",EDGE,"E14.right");var subQ2=makeQuery(id+"F0.imprint","INTERSECT",VERTEX,{"derivedFrom":[subQ1,subQ0]});Q63=makeQuery(id+"F0.imprint","IMPRINT",FACE,{"disambiguationData":[TD([[makeQuery(id+"F0.imprint","IMPRINT",EDGE,{"disambiguationData":[TD([[subQ2,-1.0]])],"derivedFrom":subQ1}),-1.0]])]});}
            var Q64;
            {var subQ0=sQuery(id+"F0.wireOp",EDGE,"E24");var subQ1=sQuery(id+"F0.wireOp",EDGE,"E13.right");var subQ2=makeQuery(id+"F0.imprint","INTERSECT",VERTEX,{"derivedFrom":[subQ1,subQ0]});Q64=makeQuery(id+"F0.imprint","IMPRINT",FACE,{"disambiguationData":[TD([[makeQuery(id+"F0.imprint","IMPRINT",EDGE,{"disambiguationData":[TD([[subQ2,-1.0]])],"derivedFrom":subQ1}),-1.0]])]});}
            var Q65;
            {var subQ0=sQuery(id+"F0.wireOp",EDGE,"E13.right");var subQ1=sQuery(id+"F0.wireOp",EDGE,"E8.top");var subQ2=makeQuery(id+"F0.imprint","INTERSECT",VERTEX,{"derivedFrom":[subQ1,subQ0]});Q65=makeQuery(id+"F0.imprint","IMPRINT",FACE,{"disambiguationData":[TD([[makeQuery(id+"F0.imprint","IMPRINT",EDGE,{"disambiguationData":[TD([[subQ2,-1.0]])],"derivedFrom":subQ1}),-1.0]])]});}
            var Q66;
            {var subQ0=sQuery(id+"F0.wireOp",EDGE,"E15.right");var subQ1=sQuery(id+"F0.wireOp",EDGE,"E8.top");var subQ2=makeQuery(id+"F0.imprint","INTERSECT",VERTEX,{"derivedFrom":[subQ1,subQ0]});Q66=makeQuery(id+"F0.imprint","IMPRINT",FACE,{"disambiguationData":[TD([[makeQuery(id+"F0.imprint","IMPRINT",EDGE,{"disambiguationData":[TD([[subQ2,-1.0]])],"derivedFrom":subQ1}),-1.0]])]});}
            var Q67;
            {var subQ0=sQuery(id+"F0.wireOp",EDGE,"E24");var subQ1=sQuery(id+"F0.wireOp",EDGE,"E15.right");var subQ2=makeQuery(id+"F0.imprint","INTERSECT",VERTEX,{"derivedFrom":[subQ1,subQ0]});Q67=makeQuery(id+"F0.imprint","IMPRINT",FACE,{"disambiguationData":[TD([[makeQuery(id+"F0.imprint","IMPRINT",EDGE,{"disambiguationData":[TD([[subQ2,-1.0]])],"derivedFrom":subQ1}),-1.0]])]});}
            var Q68;
            {var subQ0=sQuery(id+"F0.wireOp",EDGE,"E25");var subQ1=sQuery(id+"F0.wireOp",EDGE,"E16.right");var subQ2=makeQuery(id+"F0.imprint","INTERSECT",VERTEX,{"derivedFrom":[subQ1,subQ0]});Q68=makeQuery(id+"F0.imprint","IMPRINT",FACE,{"disambiguationData":[TD([[makeQuery(id+"F0.imprint","IMPRINT",EDGE,{"disambiguationData":[TD([[subQ2,-1.0]])],"derivedFrom":subQ1}),-1.0]])]});}
            var Q69;
            {var subQ0=sQuery(id+"F0.wireOp",EDGE,"E26");var subQ1=sQuery(id+"F0.wireOp",EDGE,"E17.right");var subQ2=makeQuery(id+"F0.imprint","INTERSECT",VERTEX,{"derivedFrom":[subQ1,subQ0]});Q69=makeQuery(id+"F0.imprint","IMPRINT",FACE,{"disambiguationData":[TD([[makeQuery(id+"F0.imprint","IMPRINT",EDGE,{"disambiguationData":[TD([[subQ2,-1.0]])],"derivedFrom":subQ1}),-1.0]])]});}
            var Q70;
            {var subQ0=sQuery(id+"F0.wireOp",EDGE,"E17.right");var subQ1=sQuery(id+"F0.wireOp",EDGE,"E8.top");var subQ2=makeQuery(id+"F0.imprint","INTERSECT",VERTEX,{"derivedFrom":[subQ1,subQ0]});Q70=makeQuery(id+"F0.imprint","IMPRINT",FACE,{"disambiguationData":[TD([[makeQuery(id+"F0.imprint","IMPRINT",EDGE,{"disambiguationData":[TD([[subQ2,-1.0]])],"derivedFrom":subQ1}),-1.0]])]});}
            var Q71;
            {var subQ0=sQuery(id+"F0.wireOp",EDGE,"E24");var subQ1=sQuery(id+"F0.wireOp",EDGE,"E17.right");var subQ2=makeQuery(id+"F0.imprint","INTERSECT",VERTEX,{"derivedFrom":[subQ1,subQ0]});Q71=makeQuery(id+"F0.imprint","IMPRINT",FACE,{"disambiguationData":[TD([[makeQuery(id+"F0.imprint","IMPRINT",EDGE,{"disambiguationData":[TD([[subQ2,-1.0]])],"derivedFrom":subQ1}),-1.0]])]});}
            var Q72;
            {var subQ0=sQuery(id+"F0.wireOp",EDGE,"E25");var subQ1=sQuery(id+"F0.wireOp",EDGE,"E18.right");var subQ2=makeQuery(id+"F0.imprint","INTERSECT",VERTEX,{"derivedFrom":[subQ1,subQ0]});Q72=makeQuery(id+"F0.imprint","IMPRINT",FACE,{"disambiguationData":[TD([[makeQuery(id+"F0.imprint","IMPRINT",EDGE,{"disambiguationData":[TD([[subQ2,-1.0]])],"derivedFrom":subQ1}),-1.0]])]});}
            var Q73;
            {var subQ0=sQuery(id+"F0.wireOp",EDGE,"E26");var subQ1=sQuery(id+"F0.wireOp",EDGE,"E19.right");var subQ2=makeQuery(id+"F0.imprint","INTERSECT",VERTEX,{"derivedFrom":[subQ1,subQ0]});Q73=makeQuery(id+"F0.imprint","IMPRINT",FACE,{"disambiguationData":[TD([[makeQuery(id+"F0.imprint","IMPRINT",EDGE,{"disambiguationData":[TD([[subQ2,-1.0]])],"derivedFrom":subQ1}),-1.0]])]});}
            var Q74;
            {var subQ0=sQuery(id+"F0.wireOp",EDGE,"E27");var subQ1=sQuery(id+"F0.wireOp",EDGE,"E20.right");var subQ2=makeQuery(id+"F0.imprint","INTERSECT",VERTEX,{"derivedFrom":[subQ1,subQ0]});Q74=makeQuery(id+"F0.imprint","IMPRINT",FACE,{"disambiguationData":[TD([[makeQuery(id+"F0.imprint","IMPRINT",EDGE,{"disambiguationData":[TD([[subQ2,-1.0]])],"derivedFrom":subQ1}),-1.0]])]});}
            var Q75;
            {var subQ0=sQuery(id+"F0.wireOp",EDGE,"E28");var subQ1=sQuery(id+"F0.wireOp",EDGE,"E21.right");var subQ2=makeQuery(id+"F0.imprint","INTERSECT",VERTEX,{"derivedFrom":[subQ1,subQ0]});Q75=makeQuery(id+"F0.imprint","IMPRINT",FACE,{"disambiguationData":[TD([[makeQuery(id+"F0.imprint","IMPRINT",EDGE,{"disambiguationData":[TD([[subQ2,-1.0]])],"derivedFrom":subQ1}),-1.0]])]});}
            var Q76;
            {var subQ0=sQuery(id+"F0.wireOp",EDGE,"E29");var subQ1=sQuery(id+"F0.wireOp",EDGE,"E22.right");var subQ2=makeQuery(id+"F0.imprint","INTERSECT",VERTEX,{"derivedFrom":[subQ1,subQ0]});Q76=makeQuery(id+"F0.imprint","IMPRINT",FACE,{"disambiguationData":[TD([[makeQuery(id+"F0.imprint","IMPRINT",EDGE,{"disambiguationData":[TD([[subQ2,-1.0]])],"derivedFrom":subQ1}),-1.0]])]});}
            var Q77;
            {var subQ0=sQuery(id+"F0.wireOp",EDGE,"E44");Q77=makeQuery(id+"F0.imprint","IMPRINT",FACE,{"disambiguationData":[TD([[makeQuery(id+"F0.imprint","IMPRINT",EDGE,{"derivedFrom":subQ0}),1.0]])]});}
            var Q78;
            {var subQ0=sQuery(id+"F0.wireOp",EDGE,"E35");var subQ1=sQuery(id+"F0.wireOp",EDGE,"E29");var subQ2=makeQuery(id+"F0.imprint","INTERSECT",VERTEX,{"derivedFrom":[subQ1,subQ0]});Q78=makeQuery(id+"F0.imprint","IMPRINT",FACE,{"disambiguationData":[TD([[makeQuery(id+"F0.imprint","IMPRINT",EDGE,{"disambiguationData":[TD([[subQ2,-1.0]])],"derivedFrom":subQ1}),1.0]])]});}
            var Q79;
            {var subQ0=sQuery(id+"F0.wireOp",EDGE,"E37");var subQ1=sQuery(id+"F0.wireOp",EDGE,"E2");var subQ2=makeQuery(id+"F0.imprint","INTERSECT",VERTEX,{"derivedFrom":[subQ1,subQ0]});Q79=makeQuery(id+"F0.imprint","IMPRINT",FACE,{"disambiguationData":[TD([[makeQuery(id+"F0.imprint","IMPRINT",EDGE,{"disambiguationData":[TD([[subQ2,-1.0]])],"derivedFrom":subQ1}),1.0]])]});}
            var Q80;
            {var subQ0=sQuery(id+"F0.wireOp",EDGE,"E35");var subQ1=sQuery(id+"F0.wireOp",EDGE,"E33");var subQ2=makeQuery(id+"F0.imprint","INTERSECT",VERTEX,{"derivedFrom":[subQ1,subQ0]});Q80=makeQuery(id+"F0.imprint","IMPRINT",FACE,{"disambiguationData":[TD([[makeQuery(id+"F0.imprint","IMPRINT",EDGE,{"disambiguationData":[TD([[subQ2,-1.0]])],"derivedFrom":subQ1}),-1.0]])]});}
            var Q81;
            {var subQ0=sQuery(id+"F0.wireOp",EDGE,"E40");var subQ1=sQuery(id+"F0.wireOp",EDGE,"E33");var subQ2=makeQuery(id+"F0.imprint","INTERSECT",VERTEX,{"derivedFrom":[subQ1,subQ0]});Q81=makeQuery(id+"F0.imprint","IMPRINT",FACE,{"disambiguationData":[TD([[makeQuery(id+"F0.imprint","IMPRINT",EDGE,{"disambiguationData":[TD([[subQ2,-1.0]])],"derivedFrom":subQ1}),-1.0]])]});}
            var Q82;
            {var subQ0=sQuery(id+"F0.wireOp",EDGE,"E41");var subQ1=sQuery(id+"F0.wireOp",EDGE,"E33");var subQ2=makeQuery(id+"F0.imprint","INTERSECT",VERTEX,{"derivedFrom":[subQ1,subQ0]});Q82=makeQuery(id+"F0.imprint","IMPRINT",FACE,{"disambiguationData":[TD([[makeQuery(id+"F0.imprint","IMPRINT",EDGE,{"disambiguationData":[TD([[subQ2,-1.0]])],"derivedFrom":subQ1}),-1.0]])]});}
            var Q83;
            {var subQ0=sQuery(id+"F0.wireOp",EDGE,"E40");var subQ1=sQuery(id+"F0.wireOp",EDGE,"E29");var subQ2=makeQuery(id+"F0.imprint","INTERSECT",VERTEX,{"derivedFrom":[subQ1,subQ0]});Q83=makeQuery(id+"F0.imprint","IMPRINT",FACE,{"disambiguationData":[TD([[makeQuery(id+"F0.imprint","IMPRINT",EDGE,{"disambiguationData":[TD([[subQ2,-1.0]])],"derivedFrom":subQ1}),1.0]])]});}
            var Q84;
            {var subQ0=sQuery(id+"F0.wireOp",EDGE,"E37");var subQ1=sQuery(id+"F0.wireOp",EDGE,"E29");var subQ2=makeQuery(id+"F0.imprint","INTERSECT",VERTEX,{"derivedFrom":[subQ1,subQ0]});Q84=makeQuery(id+"F0.imprint","IMPRINT",FACE,{"disambiguationData":[TD([[makeQuery(id+"F0.imprint","IMPRINT",EDGE,{"disambiguationData":[TD([[subQ2,-1.0]])],"derivedFrom":subQ1}),1.0]])]});}
            var Q85;
            {var subQ0=sQuery(id+"F0.wireOp",EDGE,"E45");var subQ1=sQuery(id+"F0.wireOp",EDGE,"E29");var subQ2=makeQuery(id+"F0.imprint","INTERSECT",VERTEX,{"derivedFrom":[subQ1,subQ0]});Q85=makeQuery(id+"F0.imprint","IMPRINT",FACE,{"disambiguationData":[TD([[makeQuery(id+"F0.imprint","IMPRINT",EDGE,{"disambiguationData":[TD([[subQ2,-1.0]])],"derivedFrom":subQ1}),1.0]])]});}
            var Q86;
            {var subQ0=sQuery(id+"F0.wireOp",EDGE,"E28");var subQ1=sQuery(id+"F0.wireOp",EDGE,"E23.right");var subQ2=makeQuery(id+"F0.imprint","INTERSECT",VERTEX,{"derivedFrom":[subQ1,subQ0]});Q86=makeQuery(id+"F0.imprint","IMPRINT",FACE,{"disambiguationData":[TD([[makeQuery(id+"F0.imprint","IMPRINT",EDGE,{"disambiguationData":[TD([[subQ2,-1.0]])],"derivedFrom":subQ1}),-1.0]])]});}
            var Q87;
            {var subQ0=sQuery(id+"F0.wireOp",EDGE,"E27");var subQ1=sQuery(id+"F0.wireOp",EDGE,"E22.right");var subQ2=makeQuery(id+"F0.imprint","INTERSECT",VERTEX,{"derivedFrom":[subQ1,subQ0]});Q87=makeQuery(id+"F0.imprint","IMPRINT",FACE,{"disambiguationData":[TD([[makeQuery(id+"F0.imprint","IMPRINT",EDGE,{"disambiguationData":[TD([[subQ2,-1.0]])],"derivedFrom":subQ1}),-1.0]])]});}
            var Q88;
            {var subQ0=sQuery(id+"F0.wireOp",EDGE,"E26");var subQ1=sQuery(id+"F0.wireOp",EDGE,"E21.right");var subQ2=makeQuery(id+"F0.imprint","INTERSECT",VERTEX,{"derivedFrom":[subQ1,subQ0]});Q88=makeQuery(id+"F0.imprint","IMPRINT",FACE,{"disambiguationData":[TD([[makeQuery(id+"F0.imprint","IMPRINT",EDGE,{"disambiguationData":[TD([[subQ2,-1.0]])],"derivedFrom":subQ1}),-1.0]])]});}
            var Q89;
            {var subQ0=sQuery(id+"F0.wireOp",EDGE,"E25");var subQ1=sQuery(id+"F0.wireOp",EDGE,"E20.right");var subQ2=makeQuery(id+"F0.imprint","INTERSECT",VERTEX,{"derivedFrom":[subQ1,subQ0]});Q89=makeQuery(id+"F0.imprint","IMPRINT",FACE,{"disambiguationData":[TD([[makeQuery(id+"F0.imprint","IMPRINT",EDGE,{"disambiguationData":[TD([[subQ2,-1.0]])],"derivedFrom":subQ1}),-1.0]])]});}
            var Q90;
            {var subQ0=sQuery(id+"F0.wireOp",EDGE,"E24");var subQ1=sQuery(id+"F0.wireOp",EDGE,"E19.right");var subQ2=makeQuery(id+"F0.imprint","INTERSECT",VERTEX,{"derivedFrom":[subQ1,subQ0]});Q90=makeQuery(id+"F0.imprint","IMPRINT",FACE,{"disambiguationData":[TD([[makeQuery(id+"F0.imprint","IMPRINT",EDGE,{"disambiguationData":[TD([[subQ2,-1.0]])],"derivedFrom":subQ1}),-1.0]])]});}
            var Q91;
            {var subQ0=sQuery(id+"F0.wireOp",EDGE,"E19.right");var subQ1=sQuery(id+"F0.wireOp",EDGE,"E8.top");var subQ2=makeQuery(id+"F0.imprint","INTERSECT",VERTEX,{"derivedFrom":[subQ1,subQ0]});Q91=makeQuery(id+"F0.imprint","IMPRINT",FACE,{"disambiguationData":[TD([[makeQuery(id+"F0.imprint","IMPRINT",EDGE,{"disambiguationData":[TD([[subQ2,-1.0]])],"derivedFrom":subQ1}),-1.0]])]});}
            var Q92;
            {var subQ0=sQuery(id+"F0.wireOp",EDGE,"E21.right");var subQ1=sQuery(id+"F0.wireOp",EDGE,"E8.top");var subQ2=makeQuery(id+"F0.imprint","INTERSECT",VERTEX,{"derivedFrom":[subQ1,subQ0]});Q92=makeQuery(id+"F0.imprint","IMPRINT",FACE,{"disambiguationData":[TD([[makeQuery(id+"F0.imprint","IMPRINT",EDGE,{"disambiguationData":[TD([[subQ2,-1.0]])],"derivedFrom":subQ1}),-1.0]])]});}
            var Q93;
            {var subQ0=sQuery(id+"F0.wireOp",EDGE,"E24");var subQ1=sQuery(id+"F0.wireOp",EDGE,"E21.right");var subQ2=makeQuery(id+"F0.imprint","INTERSECT",VERTEX,{"derivedFrom":[subQ1,subQ0]});Q93=makeQuery(id+"F0.imprint","IMPRINT",FACE,{"disambiguationData":[TD([[makeQuery(id+"F0.imprint","IMPRINT",EDGE,{"disambiguationData":[TD([[subQ2,-1.0]])],"derivedFrom":subQ1}),-1.0]])]});}
            var Q94;
            {var subQ0=sQuery(id+"F0.wireOp",EDGE,"E25");var subQ1=sQuery(id+"F0.wireOp",EDGE,"E22.right");var subQ2=makeQuery(id+"F0.imprint","INTERSECT",VERTEX,{"derivedFrom":[subQ1,subQ0]});Q94=makeQuery(id+"F0.imprint","IMPRINT",FACE,{"disambiguationData":[TD([[makeQuery(id+"F0.imprint","IMPRINT",EDGE,{"disambiguationData":[TD([[subQ2,-1.0]])],"derivedFrom":subQ1}),-1.0]])]});}
            var Q95;
            {var subQ0=sQuery(id+"F0.wireOp",EDGE,"E26");var subQ1=sQuery(id+"F0.wireOp",EDGE,"E23.right");var subQ2=makeQuery(id+"F0.imprint","INTERSECT",VERTEX,{"derivedFrom":[subQ1,subQ0]});Q95=makeQuery(id+"F0.imprint","IMPRINT",FACE,{"disambiguationData":[TD([[makeQuery(id+"F0.imprint","IMPRINT",EDGE,{"disambiguationData":[TD([[subQ2,-1.0]])],"derivedFrom":subQ1}),-1.0]])]});}
            var Q96;
            {var subQ0=sQuery(id+"F0.wireOp",EDGE,"E37");var subQ1=sQuery(id+"F0.wireOp",EDGE,"E28");var subQ2=makeQuery(id+"F0.imprint","INTERSECT",VERTEX,{"derivedFrom":[subQ1,subQ0]});Q96=makeQuery(id+"F0.imprint","IMPRINT",FACE,{"disambiguationData":[TD([[makeQuery(id+"F0.imprint","IMPRINT",EDGE,{"disambiguationData":[TD([[subQ2,-1.0]])],"derivedFrom":subQ1}),-1.0]])]});}
            var Q97;
            {var subQ0=sQuery(id+"F0.wireOp",EDGE,"E35");var subQ1=sQuery(id+"F0.wireOp",EDGE,"E28");var subQ2=makeQuery(id+"F0.imprint","INTERSECT",VERTEX,{"derivedFrom":[subQ1,subQ0]});Q97=makeQuery(id+"F0.imprint","IMPRINT",FACE,{"disambiguationData":[TD([[makeQuery(id+"F0.imprint","IMPRINT",EDGE,{"disambiguationData":[TD([[subQ2,-1.0]])],"derivedFrom":subQ1}),-1.0]])]});}
            var Q98;
            {var subQ0=sQuery(id+"F0.wireOp",EDGE,"E36");var subQ1=sQuery(id+"F0.wireOp",EDGE,"E27");var subQ2=makeQuery(id+"F0.imprint","INTERSECT",VERTEX,{"derivedFrom":[subQ1,subQ0]});Q98=makeQuery(id+"F0.imprint","IMPRINT",FACE,{"disambiguationData":[TD([[makeQuery(id+"F0.imprint","IMPRINT",EDGE,{"disambiguationData":[TD([[subQ2,-1.0]])],"derivedFrom":subQ1}),-1.0]])]});}
            var Q99;
            {var subQ0=sQuery(id+"F0.wireOp",EDGE,"E38");var subQ1=sQuery(id+"F0.wireOp",EDGE,"E27");var subQ2=makeQuery(id+"F0.imprint","INTERSECT",VERTEX,{"derivedFrom":[subQ1,subQ0]});Q99=makeQuery(id+"F0.imprint","IMPRINT",FACE,{"disambiguationData":[TD([[makeQuery(id+"F0.imprint","IMPRINT",EDGE,{"disambiguationData":[TD([[subQ2,-1.0]])],"derivedFrom":subQ1}),-1.0]])]});}
            var Q100;
            {var subQ0=sQuery(id+"F0.wireOp",EDGE,"E37");var subQ1=sQuery(id+"F0.wireOp",EDGE,"E26");var subQ2=makeQuery(id+"F0.imprint","INTERSECT",VERTEX,{"derivedFrom":[subQ1,subQ0]});Q100=makeQuery(id+"F0.imprint","IMPRINT",FACE,{"disambiguationData":[TD([[makeQuery(id+"F0.imprint","IMPRINT",EDGE,{"disambiguationData":[TD([[subQ2,-1.0]])],"derivedFrom":subQ1}),-1.0]])]});}
            var Q101;
            {var subQ0=sQuery(id+"F0.wireOp",EDGE,"E38");var subQ1=sQuery(id+"F0.wireOp",EDGE,"E25");var subQ2=makeQuery(id+"F0.imprint","INTERSECT",VERTEX,{"derivedFrom":[subQ1,subQ0]});Q101=makeQuery(id+"F0.imprint","IMPRINT",FACE,{"disambiguationData":[TD([[makeQuery(id+"F0.imprint","IMPRINT",EDGE,{"disambiguationData":[TD([[subQ2,-1.0]])],"derivedFrom":subQ1}),-1.0]])]});}
            var Q102;
            {var subQ0=sQuery(id+"F0.wireOp",EDGE,"E24");var subQ1=sQuery(id+"F0.wireOp",EDGE,"E23.right");var subQ2=makeQuery(id+"F0.imprint","INTERSECT",VERTEX,{"derivedFrom":[subQ1,subQ0]});Q102=makeQuery(id+"F0.imprint","IMPRINT",FACE,{"disambiguationData":[TD([[makeQuery(id+"F0.imprint","IMPRINT",EDGE,{"disambiguationData":[TD([[subQ2,-1.0]])],"derivedFrom":subQ1}),-1.0]])]});}
            var Q103;
            {var subQ0=sQuery(id+"F0.wireOp",EDGE,"E23.right");var subQ1=sQuery(id+"F0.wireOp",EDGE,"E8.top");var subQ2=makeQuery(id+"F0.imprint","INTERSECT",VERTEX,{"derivedFrom":[subQ1,subQ0]});Q103=makeQuery(id+"F0.imprint","IMPRINT",FACE,{"disambiguationData":[TD([[makeQuery(id+"F0.imprint","IMPRINT",EDGE,{"disambiguationData":[TD([[subQ2,-1.0]])],"derivedFrom":subQ1}),-1.0]])]});}
            var Q104;
            {var subQ0=sQuery(id+"F0.wireOp",EDGE,"E38");var subQ1=sQuery(id+"F0.wireOp",EDGE,"E8.top");var subQ2=makeQuery(id+"F0.imprint","INTERSECT",VERTEX,{"derivedFrom":[subQ1,subQ0]});Q104=makeQuery(id+"F0.imprint","IMPRINT",FACE,{"disambiguationData":[TD([[makeQuery(id+"F0.imprint","IMPRINT",EDGE,{"disambiguationData":[TD([[subQ2,-1.0]])],"derivedFrom":subQ1}),-1.0]])]});}
            var Q105;
            {var subQ0=sQuery(id+"F0.wireOp",EDGE,"E37");var subQ1=sQuery(id+"F0.wireOp",EDGE,"E24");var subQ2=makeQuery(id+"F0.imprint","INTERSECT",VERTEX,{"derivedFrom":[subQ1,subQ0]});Q105=makeQuery(id+"F0.imprint","IMPRINT",FACE,{"disambiguationData":[TD([[makeQuery(id+"F0.imprint","IMPRINT",EDGE,{"disambiguationData":[TD([[subQ2,-1.0]])],"derivedFrom":subQ1}),-1.0]])]});}
            var Q106;
            {var subQ0=sQuery(id+"F0.wireOp",EDGE,"E36");var subQ1=sQuery(id+"F0.wireOp",EDGE,"E25");var subQ2=makeQuery(id+"F0.imprint","INTERSECT",VERTEX,{"derivedFrom":[subQ1,subQ0]});Q106=makeQuery(id+"F0.imprint","IMPRINT",FACE,{"disambiguationData":[TD([[makeQuery(id+"F0.imprint","IMPRINT",EDGE,{"disambiguationData":[TD([[subQ2,-1.0]])],"derivedFrom":subQ1}),-1.0]])]});}
            var Q107;
            {var subQ0=sQuery(id+"F0.wireOp",EDGE,"E35");var subQ1=sQuery(id+"F0.wireOp",EDGE,"E26");var subQ2=makeQuery(id+"F0.imprint","INTERSECT",VERTEX,{"derivedFrom":[subQ1,subQ0]});Q107=makeQuery(id+"F0.imprint","IMPRINT",FACE,{"disambiguationData":[TD([[makeQuery(id+"F0.imprint","IMPRINT",EDGE,{"disambiguationData":[TD([[subQ2,-1.0]])],"derivedFrom":subQ1}),-1.0]])]});}
            var Q108;
            {var subQ0=sQuery(id+"F0.wireOp",EDGE,"E34");var subQ1=sQuery(id+"F0.wireOp",EDGE,"E27");var subQ2=makeQuery(id+"F0.imprint","INTERSECT",VERTEX,{"derivedFrom":[subQ1,subQ0]});Q108=makeQuery(id+"F0.imprint","IMPRINT",FACE,{"disambiguationData":[TD([[makeQuery(id+"F0.imprint","IMPRINT",EDGE,{"disambiguationData":[TD([[subQ2,-1.0]])],"derivedFrom":subQ1}),-1.0]])]});}
            var Q109;
            {var subQ0=sQuery(id+"F0.wireOp",EDGE,"E40");var subQ1=sQuery(id+"F0.wireOp",EDGE,"E28");var subQ2=makeQuery(id+"F0.imprint","INTERSECT",VERTEX,{"derivedFrom":[subQ1,subQ0]});Q109=makeQuery(id+"F0.imprint","IMPRINT",FACE,{"disambiguationData":[TD([[makeQuery(id+"F0.imprint","IMPRINT",EDGE,{"disambiguationData":[TD([[subQ2,-1.0]])],"derivedFrom":subQ1}),-1.0]])]});}
            var Q110;
            {var subQ0=sQuery(id+"F0.wireOp",EDGE,"E39");var subQ1=sQuery(id+"F0.wireOp",EDGE,"E27");var subQ2=makeQuery(id+"F0.imprint","INTERSECT",VERTEX,{"derivedFrom":[subQ1,subQ0]});Q110=makeQuery(id+"F0.imprint","IMPRINT",FACE,{"disambiguationData":[TD([[makeQuery(id+"F0.imprint","IMPRINT",EDGE,{"disambiguationData":[TD([[subQ2,-1.0]])],"derivedFrom":subQ1}),-1.0]])]});}
            var Q111;
            {var subQ0=sQuery(id+"F0.wireOp",EDGE,"E41");var subQ1=sQuery(id+"F0.wireOp",EDGE,"E28");var subQ2=makeQuery(id+"F0.imprint","INTERSECT",VERTEX,{"derivedFrom":[subQ1,subQ0]});Q111=makeQuery(id+"F0.imprint","IMPRINT",FACE,{"disambiguationData":[TD([[makeQuery(id+"F0.imprint","IMPRINT",EDGE,{"disambiguationData":[TD([[subQ2,-1.0]])],"derivedFrom":subQ1}),-1.0]])]});}
            var Q112;
            {var subQ0=sQuery(id+"F0.wireOp",EDGE,"E40");var subQ1=sQuery(id+"F0.wireOp",EDGE,"E26");var subQ2=makeQuery(id+"F0.imprint","INTERSECT",VERTEX,{"derivedFrom":[subQ1,subQ0]});Q112=makeQuery(id+"F0.imprint","IMPRINT",FACE,{"disambiguationData":[TD([[makeQuery(id+"F0.imprint","IMPRINT",EDGE,{"disambiguationData":[TD([[subQ2,-1.0]])],"derivedFrom":subQ1}),-1.0]])]});}
            var Q113;
            {var subQ0=sQuery(id+"F0.wireOp",EDGE,"E41");var subQ1=sQuery(id+"F0.wireOp",EDGE,"E26");var subQ2=makeQuery(id+"F0.imprint","INTERSECT",VERTEX,{"derivedFrom":[subQ1,subQ0]});Q113=makeQuery(id+"F0.imprint","IMPRINT",FACE,{"disambiguationData":[TD([[makeQuery(id+"F0.imprint","IMPRINT",EDGE,{"disambiguationData":[TD([[subQ2,-1.0]])],"derivedFrom":subQ1}),-1.0]])]});}
            var Q114;
            {var subQ0=sQuery(id+"F0.wireOp",EDGE,"E39");var subQ1=sQuery(id+"F0.wireOp",EDGE,"E25");var subQ2=makeQuery(id+"F0.imprint","INTERSECT",VERTEX,{"derivedFrom":[subQ1,subQ0]});Q114=makeQuery(id+"F0.imprint","IMPRINT",FACE,{"disambiguationData":[TD([[makeQuery(id+"F0.imprint","IMPRINT",EDGE,{"disambiguationData":[TD([[subQ2,-1.0]])],"derivedFrom":subQ1}),-1.0]])]});}
            var Q115;
            {var subQ0=sQuery(id+"F0.wireOp",EDGE,"E34");var subQ1=sQuery(id+"F0.wireOp",EDGE,"E25");var subQ2=makeQuery(id+"F0.imprint","INTERSECT",VERTEX,{"derivedFrom":[subQ1,subQ0]});Q115=makeQuery(id+"F0.imprint","IMPRINT",FACE,{"disambiguationData":[TD([[makeQuery(id+"F0.imprint","IMPRINT",EDGE,{"disambiguationData":[TD([[subQ2,-1.0]])],"derivedFrom":subQ1}),-1.0]])]});}
            var Q116;
            {var subQ0=sQuery(id+"F0.wireOp",EDGE,"E40");var subQ1=sQuery(id+"F0.wireOp",EDGE,"E24");var subQ2=makeQuery(id+"F0.imprint","INTERSECT",VERTEX,{"derivedFrom":[subQ1,subQ0]});Q116=makeQuery(id+"F0.imprint","IMPRINT",FACE,{"disambiguationData":[TD([[makeQuery(id+"F0.imprint","IMPRINT",EDGE,{"disambiguationData":[TD([[subQ2,-1.0]])],"derivedFrom":subQ1}),-1.0]])]});}
            var Q117;
            {var subQ0=sQuery(id+"F0.wireOp",EDGE,"E41");var subQ1=sQuery(id+"F0.wireOp",EDGE,"E24");var subQ2=makeQuery(id+"F0.imprint","INTERSECT",VERTEX,{"derivedFrom":[subQ1,subQ0]});Q117=makeQuery(id+"F0.imprint","IMPRINT",FACE,{"disambiguationData":[TD([[makeQuery(id+"F0.imprint","IMPRINT",EDGE,{"disambiguationData":[TD([[subQ2,-1.0]])],"derivedFrom":subQ1}),-1.0]])]});}
            var Q118;
            {var subQ0=sQuery(id+"F0.wireOp",EDGE,"E39");var subQ1=sQuery(id+"F0.wireOp",EDGE,"E8.top");var subQ2=makeQuery(id+"F0.imprint","INTERSECT",VERTEX,{"derivedFrom":[subQ1,subQ0]});Q118=makeQuery(id+"F0.imprint","IMPRINT",FACE,{"disambiguationData":[TD([[makeQuery(id+"F0.imprint","IMPRINT",EDGE,{"disambiguationData":[TD([[subQ2,-1.0]])],"derivedFrom":subQ1}),-1.0]])]});}
            var Q119;
            {var subQ0=sQuery(id+"F0.wireOp",EDGE,"E34");var subQ1=sQuery(id+"F0.wireOp",EDGE,"E8.top");var subQ2=makeQuery(id+"F0.imprint","INTERSECT",VERTEX,{"derivedFrom":[subQ1,subQ0]});Q119=makeQuery(id+"F0.imprint","IMPRINT",FACE,{"disambiguationData":[TD([[makeQuery(id+"F0.imprint","IMPRINT",EDGE,{"disambiguationData":[TD([[subQ2,-1.0]])],"derivedFrom":subQ1}),-1.0]])]});}
            var Q120;
            {var subQ0=sQuery(id+"F0.wireOp",EDGE,"E35");var subQ1=sQuery(id+"F0.wireOp",EDGE,"E24");var subQ2=makeQuery(id+"F0.imprint","INTERSECT",VERTEX,{"derivedFrom":[subQ1,subQ0]});Q120=makeQuery(id+"F0.imprint","IMPRINT",FACE,{"disambiguationData":[TD([[makeQuery(id+"F0.imprint","IMPRINT",EDGE,{"disambiguationData":[TD([[subQ2,-1.0]])],"derivedFrom":subQ1}),-1.0]])]});}
            var Q121;
            {var subQ0=sQuery(id+"F0.wireOp",EDGE,"E36");var subQ1=sQuery(id+"F0.wireOp",EDGE,"E8.top");var subQ2=makeQuery(id+"F0.imprint","INTERSECT",VERTEX,{"derivedFrom":[subQ1,subQ0]});Q121=makeQuery(id+"F0.imprint","IMPRINT",FACE,{"disambiguationData":[TD([[makeQuery(id+"F0.imprint","IMPRINT",EDGE,{"disambiguationData":[TD([[subQ2,-1.0]])],"derivedFrom":subQ1}),-1.0]])]});}
            var Q122;
            {var subQ5=sQuery(id+"F0.wireOp",EDGE,"E10.bottom");Q122=makeQuery(id+"F0.imprint","IMPRINT",FACE,{"disambiguationData":[TD([[makeQuery(id+"F0.imprint","IMPRINT",EDGE,{"derivedFrom":subQ5}),1.0]])]});}
            var Q123;
            {var subQ5=sQuery(id+"F0.wireOp",EDGE,"E12.bottom");Q123=makeQuery(id+"F0.imprint","IMPRINT",FACE,{"disambiguationData":[TD([[makeQuery(id+"F0.imprint","IMPRINT",EDGE,{"derivedFrom":subQ5}),1.0]])]});}
            var Q124;
            {var subQ5=sQuery(id+"F0.wireOp",EDGE,"E14.bottom");Q124=makeQuery(id+"F0.imprint","IMPRINT",FACE,{"disambiguationData":[TD([[makeQuery(id+"F0.imprint","IMPRINT",EDGE,{"derivedFrom":subQ5}),1.0]])]});}
            var Q125;
            {var subQ5=sQuery(id+"F0.wireOp",EDGE,"E16.bottom");Q125=makeQuery(id+"F0.imprint","IMPRINT",FACE,{"disambiguationData":[TD([[makeQuery(id+"F0.imprint","IMPRINT",EDGE,{"derivedFrom":subQ5}),1.0]])]});}
            var Q126;
            {var subQ5=sQuery(id+"F0.wireOp",EDGE,"E18.bottom");Q126=makeQuery(id+"F0.imprint","IMPRINT",FACE,{"disambiguationData":[TD([[makeQuery(id+"F0.imprint","IMPRINT",EDGE,{"derivedFrom":subQ5}),1.0]])]});}
            var Q127;
            {var subQ5=sQuery(id+"F0.wireOp",EDGE,"E20.bottom");Q127=makeQuery(id+"F0.imprint","IMPRINT",FACE,{"disambiguationData":[TD([[makeQuery(id+"F0.imprint","IMPRINT",EDGE,{"derivedFrom":subQ5}),1.0]])]});}
            var Q128;
            {var subQ5=sQuery(id+"F0.wireOp",EDGE,"E22.bottom");Q128=makeQuery(id+"F0.imprint","IMPRINT",FACE,{"disambiguationData":[TD([[makeQuery(id+"F0.imprint","IMPRINT",EDGE,{"derivedFrom":subQ5}),1.0]])]});}
            var Q129;
            {var subQ3=sQuery(id+"F0.wireOp",EDGE,"E45");var subQ5=sQuery(id+"F0.wireOp",EDGE,"E8.top");var subQ7=makeQuery(id+"F0.imprint","INTERSECT",VERTEX,{"derivedFrom":[subQ5,subQ3]});Q129=makeQuery(id+"F0.imprint","IMPRINT",FACE,{"disambiguationData":[TD([[makeQuery(id+"F0.imprint","IMPRINT",EDGE,{"disambiguationData":[TD([[subQ7,-1.0]])],"derivedFrom":subQ5}),1.0]])]});}
            var Q130;
            {var subQ0=sQuery(id+"F0.wireOp",EDGE,"E37");var subQ1=sQuery(id+"F0.wireOp",EDGE,"E8.bottom");var subQ2=makeQuery(id+"F0.imprint","INTERSECT",VERTEX,{"derivedFrom":[subQ1,subQ0]});Q130=makeQuery(id+"F0.imprint","IMPRINT",FACE,{"disambiguationData":[TD([[makeQuery(id+"F0.imprint","IMPRINT",EDGE,{"disambiguationData":[TD([[subQ2,-1.0]])],"derivedFrom":subQ1}),-1.0]])]});}
            var Q131;
            {var subQ0=sQuery(id+"F0.wireOp",EDGE,"E35");var subQ1=sQuery(id+"F0.wireOp",EDGE,"E8.bottom");var subQ2=makeQuery(id+"F0.imprint","INTERSECT",VERTEX,{"derivedFrom":[subQ1,subQ0]});Q131=makeQuery(id+"F0.imprint","IMPRINT",FACE,{"disambiguationData":[TD([[makeQuery(id+"F0.imprint","IMPRINT",EDGE,{"disambiguationData":[TD([[subQ2,-1.0]])],"derivedFrom":subQ1}),-1.0]])]});}
            var Q132;
            {var subQ0=sQuery(id+"F0.wireOp",EDGE,"E34");var subQ1=sQuery(id+"F0.wireOp",EDGE,"E8.bottom");var subQ2=makeQuery(id+"F0.imprint","INTERSECT",VERTEX,{"derivedFrom":[subQ1,subQ0]});Q132=makeQuery(id+"F0.imprint","IMPRINT",FACE,{"disambiguationData":[TD([[makeQuery(id+"F0.imprint","IMPRINT",EDGE,{"disambiguationData":[TD([[subQ2,1.0]])],"derivedFrom":subQ1}),-1.0]])]});}
            var Q133;
            {var subQ0=sQuery(id+"F0.wireOp",EDGE,"E39");var subQ1=sQuery(id+"F0.wireOp",EDGE,"E8.bottom");var subQ2=makeQuery(id+"F0.imprint","INTERSECT",VERTEX,{"derivedFrom":[subQ1,subQ0]});Q133=makeQuery(id+"F0.imprint","IMPRINT",FACE,{"disambiguationData":[TD([[makeQuery(id+"F0.imprint","IMPRINT",EDGE,{"disambiguationData":[TD([[subQ2,1.0]])],"derivedFrom":subQ1}),-1.0]])]});}
            var Q134;
            {var subQ1=sQuery(id+"F0.wireOp",EDGE,"E0.right");var subQ3=sQuery(id+"F0.wireOp",EDGE,"E24");var subQ4=makeQuery(id+"F0.imprint","INTERSECT",VERTEX,{"derivedFrom":[subQ1,subQ3]});Q134=makeQuery(id+"F0.imprint","IMPRINT",FACE,{"disambiguationData":[TD([[makeQuery(id+"F0.imprint","IMPRINT",EDGE,{"disambiguationData":[TD([[subQ4,-1.0]])],"derivedFrom":subQ3}),1.0]])]});}
            var Q135;
            {var subQ0=sQuery(id+"F0.wireOp",EDGE,"E25");var subQ1=sQuery(id+"F0.wireOp",EDGE,"E0.right");var subQ2=makeQuery(id+"F0.imprint","INTERSECT",VERTEX,{"derivedFrom":[subQ1,subQ0]});Q135=makeQuery(id+"F0.imprint","IMPRINT",FACE,{"disambiguationData":[TD([[makeQuery(id+"F0.imprint","IMPRINT",EDGE,{"disambiguationData":[TD([[subQ2,1.0]])],"derivedFrom":subQ1}),-1.0]])]});}
            var Q136;
            {var subQ0=sQuery(id+"F0.wireOp",EDGE,"E27");var subQ1=sQuery(id+"F0.wireOp",EDGE,"E0.right");var subQ2=makeQuery(id+"F0.imprint","INTERSECT",VERTEX,{"derivedFrom":[subQ1,subQ0]});Q136=makeQuery(id+"F0.imprint","IMPRINT",FACE,{"disambiguationData":[TD([[makeQuery(id+"F0.imprint","IMPRINT",EDGE,{"disambiguationData":[TD([[subQ2,1.0]])],"derivedFrom":subQ1}),-1.0]])]});}
            var Q137;
            {var subQ0=sQuery(id+"F0.wireOp",EDGE,"E29");var subQ1=sQuery(id+"F0.wireOp",EDGE,"E0.right");var subQ2=makeQuery(id+"F0.imprint","INTERSECT",VERTEX,{"derivedFrom":[subQ1,subQ0]});Q137=makeQuery(id+"F0.imprint","IMPRINT",FACE,{"disambiguationData":[TD([[makeQuery(id+"F0.imprint","IMPRINT",EDGE,{"disambiguationData":[TD([[subQ2,1.0]])],"derivedFrom":subQ1}),-1.0]])]});}
            var Q138;
            {var subQ0=sQuery(id+"F0.wireOp",EDGE,"E1");var subQ1=sQuery(id+"F0.wireOp",EDGE,"E0.right");var subQ2=makeQuery(id+"F0.imprint","INTERSECT",VERTEX,{"derivedFrom":[subQ1,subQ0]});Q138=makeQuery(id+"F0.imprint","IMPRINT",FACE,{"disambiguationData":[TD([[makeQuery(id+"F0.imprint","IMPRINT",EDGE,{"disambiguationData":[TD([[subQ2,-1.0]])],"derivedFrom":subQ1}),-1.0]])]});}
            var Q139;
            {var subQ0=sQuery(id+"F0.wireOp",EDGE,"E39");var subQ1=sQuery(id+"F0.wireOp",EDGE,"E1");var subQ2=makeQuery(id+"F0.imprint","INTERSECT",VERTEX,{"derivedFrom":[subQ1,subQ0]});Q139=makeQuery(id+"F0.imprint","IMPRINT",FACE,{"disambiguationData":[TD([[makeQuery(id+"F0.imprint","IMPRINT",EDGE,{"disambiguationData":[TD([[subQ2,-1.0]])],"derivedFrom":subQ1}),1.0]])]});}
            var Q140;
            {var subQ0=sQuery(id+"F0.wireOp",EDGE,"E34");var subQ1=sQuery(id+"F0.wireOp",EDGE,"E1");var subQ2=makeQuery(id+"F0.imprint","INTERSECT",VERTEX,{"derivedFrom":[subQ1,subQ0]});Q140=makeQuery(id+"F0.imprint","IMPRINT",FACE,{"disambiguationData":[TD([[makeQuery(id+"F0.imprint","IMPRINT",EDGE,{"disambiguationData":[TD([[subQ2,-1.0]])],"derivedFrom":subQ1}),1.0]])]});}
            var Q141;
            {var subQ0=sQuery(id+"F0.wireOp",EDGE,"E46");var subQ1=sQuery(id+"F0.wireOp",EDGE,"E2");var subQ2=makeQuery(id+"F0.imprint","INTERSECT",VERTEX,{"derivedFrom":[subQ1,subQ0]});Q141=makeQuery(id+"F0.imprint","IMPRINT",FACE,{"disambiguationData":[TD([[makeQuery(id+"F0.imprint","IMPRINT",EDGE,{"disambiguationData":[TD([[subQ2,1.0]])],"derivedFrom":subQ1}),1.0]])]});}
            var Q142;
            {var subQ0=sQuery(id+"F0.wireOp",EDGE,"E30");var subQ1=sQuery(id+"F0.wireOp",EDGE,"E4");var subQ2=makeQuery(id+"F0.imprint","INTERSECT",VERTEX,{"derivedFrom":[subQ1,subQ0]});Q142=makeQuery(id+"F0.imprint","IMPRINT",FACE,{"disambiguationData":[TD([[makeQuery(id+"F0.imprint","IMPRINT",EDGE,{"disambiguationData":[TD([[subQ2,1.0]])],"derivedFrom":subQ1}),1.0]])]});}
            var Q143;
            {var subQ0=sQuery(id+"F0.wireOp",EDGE,"E22.right");var subQ1=sQuery(id+"F0.wireOp",EDGE,"E3");var subQ2=makeQuery(id+"F0.imprint","INTERSECT",VERTEX,{"derivedFrom":[subQ1,subQ0]});Q143=makeQuery(id+"F0.imprint","IMPRINT",FACE,{"disambiguationData":[TD([[makeQuery(id+"F0.imprint","IMPRINT",EDGE,{"disambiguationData":[TD([[subQ2,1.0]])],"derivedFrom":subQ1}),1.0]])]});}
            extrude(context, id + "F2", {"entities" : qUnion([Q0, Q1, Q2, Q3, Q4, Q5, Q6, Q7, Q8, Q9, Q10, Q11, Q12, Q13, Q14, Q15, Q16, Q17, Q18, Q19, Q20, Q21, Q22, Q23, Q24, Q25, Q26, Q27, Q28, Q29, Q30, Q31, Q32, Q33, Q34, Q35, Q36, Q37, Q38, Q39, Q40, Q41, Q42, Q43, Q44, Q45, Q46, Q47, Q48, Q49, Q50, Q51, Q52, Q53, Q54, Q55, Q56, Q57, Q58, Q59, Q60, Q61, Q62, Q63, Q64, Q65, Q66, Q67, Q68, Q69, Q70, Q71, Q72, Q73, Q74, Q75, Q76, Q77, Q78, Q79, Q80, Q81, Q82, Q83, Q84, Q85, Q86, Q87, Q88, Q89, Q90, Q91, Q92, Q93, Q94, Q95, Q96, Q97, Q98, Q99, Q100, Q101, Q102, Q103, Q104, Q105, Q106, Q107, Q108, Q109, Q110, Q111, Q112, Q113, Q114, Q115, Q116, Q117, Q118, Q119, Q120, Q121, Q122, Q123, Q124, Q125, Q126, Q127, Q128, Q129, Q130, Q131, Q132, Q133, Q134, Q135, Q136, Q137, Q138, Q139, Q140, Q141, Q142, Q143]), "depth" : 25 * mm});
        }
    });
